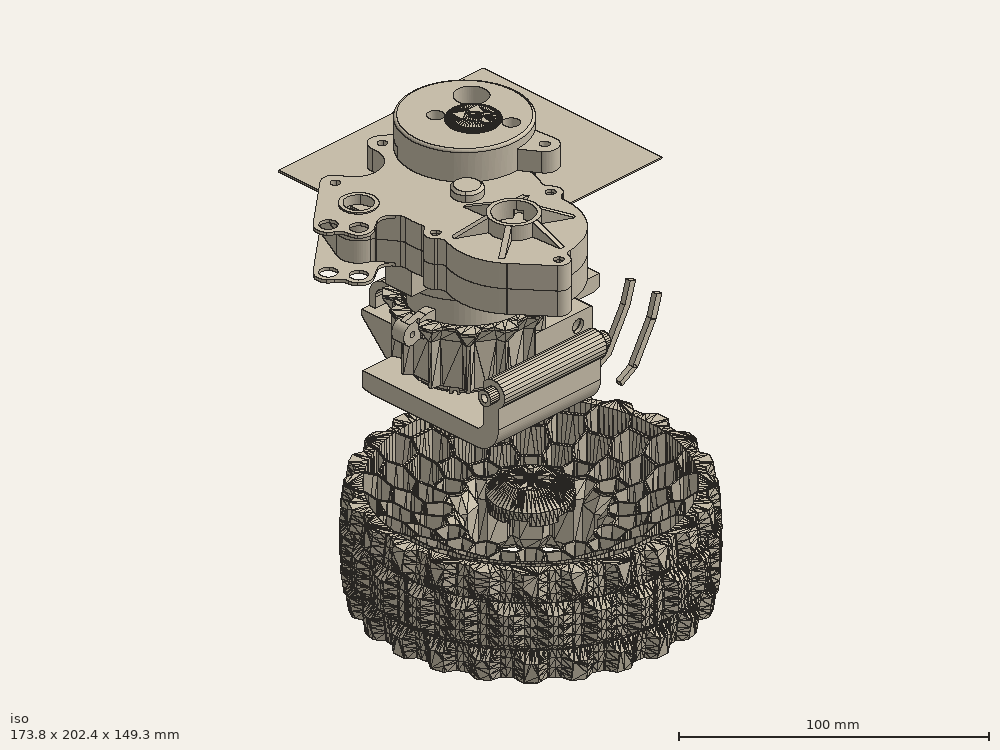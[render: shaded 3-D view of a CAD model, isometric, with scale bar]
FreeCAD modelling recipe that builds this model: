
FCSTD DOCUMENT  (FreeCAD 0.20R29410 (Git))
Label: MonsterBeetleParts
License: All rights reserved
LicenseURL: http://en.wikipedia.org/wiki/All_rights_reserved
objects: Sketcher::SketchObject×70, PartDesign::Pad×48, PartDesign::Pocket×42, Part::Feature×25, PartDesign::Fillet×22, PartDesign::Body×19, Mesh::Feature×13, Part::Box×12, PartDesign::FeatureBase×10, Part::FeaturePython×6, PartDesign::Chamfer×5, Part::MultiFuse×5, App::MeasureDistance×4, App::Part×4, App::DocumentObjectGroup×1
note: 381 computed .brp shape members not serialized (recipe doc carries the construction recipe); baked Part::Feature solids carry a one-line shape summary decoded from their .brp

FEATURE [Sketcher::SketchObject] Sketch
  FullyConstrained = true
  MapMode = 5
  Placement = pos=(0,0,0) rot=(1,0,0;1.5708rad)
  Support = -> [XZ_Plane]
  sketch-geometry (21):
    g0: Circle CenterX=0 CenterY=0 CenterZ=0 NormalX=0 NormalY=0 NormalZ=1 AngleXU=0 Radius=1.55
    g1: Circle CenterX=20 CenterY=0 CenterZ=0 NormalX=0 NormalY=0 NormalZ=1 AngleXU=0 Radius=1.55
    g2: Circle CenterX=-3 CenterY=9 CenterZ=0 NormalX=0 NormalY=0 NormalZ=1 AngleXU=0 Radius=1.05
    g3: Circle CenterX=17 CenterY=9 CenterZ=0 NormalX=0 NormalY=0 NormalZ=1 AngleXU=0 Radius=1.05
    g4: Circle CenterX=-28 CenterY=20 CenterZ=0 NormalX=0 NormalY=0 NormalZ=1 AngleXU=0 Radius=1.05
    g5: ArcOfCircle CenterX=20 CenterY=0 CenterZ=0 NormalX=0 NormalY=0 NormalZ=1 AngleXU=0 Radius=5 StartAngle=4.71239 EndAngle=7.35715
    g6: ArcOfCircle CenterX=0 CenterY=0 CenterZ=0 NormalX=0 NormalY=0 NormalZ=1 AngleXU=0 Radius=5 StartAngle=3.86723 EndAngle=4.71239
    g7: LineSegment StartX=2e-16 StartY=-5 StartZ=0 EndX=20 EndY=-5 EndZ=0
    g8: ArcOfCircle CenterX=17 CenterY=9 CenterZ=0 NormalX=0 NormalY=0 NormalZ=1 AngleXU=0 Radius=3 StartAngle=5.89015 EndAngle=8.82416
    g9: ArcOfCircle CenterX=21.6188 CenterY=7.08502 CenterZ=0 NormalX=0 NormalY=0 NormalZ=1 AngleXU=0 Radius=2 StartAngle=2.74856 EndAngle=4.21556
    g10: LineSegment StartX=20.6655 StartY=5.32683 StartZ=0 EndX=22.3832 EndY=4.3955 EndZ=0
    g11: ArcOfCircle CenterX=12.8751 CenterY=11.8258 CenterZ=0 NormalX=0 NormalY=0 NormalZ=1 AngleXU=0 Radius=2 StartAngle=4.21556 EndAngle=5.68257
    g12: ArcOfCircle CenterX=-20 CenterY=16 CenterZ=0 NormalX=0 NormalY=0 NormalZ=1 AngleXU=0 Radius=10 StartAngle=1.07397 EndAngle=1.84246
    g13: LineSegment StartX=-20 StartY=26 StartZ=0 EndX=20 EndY=26 EndZ=0
    g14: LineSegment StartX=-15.2336 StartY=24.791 StartZ=0 EndX=11.9218 EndY=10.0676 EndZ=0
    g15: LineSegment StartX=11.9218 StartY=10.0676 StartZ=0 EndX=20.6655 EndY=5.32683 EndZ=0
    g16: LineSegment StartX=-22.6834 StartY=25.6332 StartZ=0 EndX=-29.0734 EndY=23.8533 EndZ=0
    g17: ArcOfCircle CenterX=-28 CenterY=20 CenterZ=0 NormalX=0 NormalY=0 NormalZ=1 AngleXU=0 Radius=4 StartAngle=1.84246 EndAngle=5.19363
    g18: ArcOfCircle CenterX=-23.9246 CenterY=12.1957 CenterZ=0 NormalX=0 NormalY=0 NormalZ=1 AngleXU=0 Radius=4.80428 StartAngle=0.725635 EndAngle=2.05204
    g19: LineSegment StartX=-20.3307 StartY=15.3839 StartZ=0 EndX=-3.74039 EndY=-3.31805 EndZ=0
    g20: LineSegment StartX=-23.9246 StartY=17 StartZ=0 EndX=20 EndY=17 EndZ=0
  constraints (56):
    c: PointOnObject(g1,g-1)
    c: Equal(g0,g1)
    c: Diameter(g0) = 3.1
    c: Equal(g2,g3)
    c: Diameter(g2) = 2.1
    c: Diameter(g4) = 2.1
    c: Distance(g0,g1) = 20
    c: Horizontal(g3,g2)
    c: Distance(g3,g2) = 20
    c: DistanceX(g2,g0) = 3
    c: DistanceY(g0,g2) = 9
    c: DistanceY(g0,g4) = 20
    c: DistanceX(g4,g1) = 48
    c: DistanceX(g4,g2) = 25
    c: DistanceY(g2,g4) = 11
    c: Coincident(g5,g1)
    c: Distance(g1,g5) = 5
    c: Coincident(g6,g0)
    c: Distance(g0,g6) = 5
    c: Tangent(g7,g5) = -1.5708
    c: Tangent(g7,g6) = -1.5708
    c: Coincident(g8,g3)
    c: Tangent(g10,g5) = 1.5708
    c: Tangent(g10,g9) = -1.5708
    c: Distance(g9,g9) = 2
    c: Tangent(g8,g9) = 1.5708
    c: Distance(g11,g11) = 2
    c: Distance(g3,g8) = 3
    c: Tangent(g8,g11) = 1.5708
    c: Horizontal(g13)
    c: Tangent(g13,g12)
    c: Vertical(g13,g1)
    c: Distance(g13) = 40
    c: Tangent(g14,g11) = -1.5708
    c: Tangent(g14,g12) = 1.5708
    c: Coincident(g15,g11)
    c: Coincident(g15,g9)
    c: Tangent(g15,g11)
    c: Tangent(g15,g10)
    c: Distance(g13,g1) = 26
    c: Distance(g12,g12) = 10
    c: Coincident(g17,g4)
    c: Tangent(g16,g12) = -1.5708
    c: Tangent(g17,g16) = -1.5708
    c: Distance(g4,g16) = 4
    c: Tangent(g18,g17) = 1.5708
    c: Tangent(g19,g6) = -1.5708
    c: Tangent(g19,g18) = 1.5708
    c: PointOnObject(g20,g18)
    c: Horizontal(g20)
    c: Vertical(g20,g1)
    c: Tangent(g20,g18)
    c: Distance(g19) = 25
    c: Distance(g20,g1) = 17
    c: PointOnObject(g13,g12)
    c: Coincident(g0,g-1)
FEATURE [PartDesign::Pad] Pad
  Direction = (1,1,1)
  Length = 3.5
  Length2 = 100
  Placement = pos=(0,0,0) rot=(1,0,0;1.5708rad)
  Profile = -> Sketch
  Type = 0
FEATURE [Sketcher::SketchObject] Sketch001
  ExternalGeometry = -> [Pad]
  FullyConstrained = true
  MapMode = 5
  Placement = pos=(0,-3.5,8e-16) rot=(1,0,0;1.5708rad)
  Support = -> [Pad]
  sketch-geometry (8):
    g0: ArcOfCircle CenterX=-28 CenterY=20 CenterZ=0 NormalX=0 NormalY=0 NormalZ=1 AngleXU=0 Radius=4 StartAngle=5.867 EndAngle=7.19835
    g1: Circle CenterX=0 CenterY=0 CenterZ=0 NormalX=0 NormalY=0 NormalZ=1 AngleXU=0 Radius=3
    g2: Circle CenterX=20 CenterY=0 CenterZ=0 NormalX=0 NormalY=0 NormalZ=1 AngleXU=0 Radius=3
    g3: ArcOfCircle CenterX=-24.9517 CenterY=23.9633 CenterZ=0 NormalX=0 NormalY=0 NormalZ=1 AngleXU=0 Radius=1 StartAngle=1.84246 EndAngle=4.05676
    g4: ArcOfCircle CenterX=-23.4268 CenterY=17.9786 CenterZ=0 NormalX=0 NormalY=0 NormalZ=1 AngleXU=0 Radius=1 StartAngle=2.7254 EndAngle=4.62652
    g5: LineSegment StartX=-29.0734 StartY=23.8533 StartZ=0 EndX=-25.2201 EndY=24.9267 EndZ=0
    g6: ArcOfCircle CenterX=-23.9246 CenterY=12.1957 CenterZ=0 NormalX=0 NormalY=0 NormalZ=1 AngleXU=0 Radius=4.80428 StartAngle=1.48492 EndAngle=2.05204
    g7: ArcOfCircle CenterX=-28 CenterY=20 CenterZ=0 NormalX=0 NormalY=0 NormalZ=1 AngleXU=0 Radius=4 StartAngle=1.84246 EndAngle=5.19363
  constraints (21):
    c: Coincident(g0,g-3)
    c: Equal(g0,g-6)
    c: Coincident(g1,g-1)
    c: Coincident(g2,g-5)
    c: Equal(g1,g2)
    c: Diameter(g1) = 6
    c: PointOnObject(g3,g-8)
    c: Tangent(g3,g-8)
    c: Distance(g3,g3) = 1
    c: PointOnObject(g4,g-7)
    c: Tangent(g4,g-7)
    c: Distance(g4,g4) = 1
    c: Coincident(g5,g3)
    c: Coincident(g6,g-7)
    c: Coincident(g6,g4)
    c: Tangent(g0,g4) = 1.5708
    c: Coincident(g7,g6)
    c: Equal(g0,g7)
    c: Tangent(g0,g3) = 1.5708
    c: Coincident(g0,g7)
    c: Tangent(g7,g5) = 1.5708
FEATURE [PartDesign::Pocket] Pocket
  BaseFeature = -> Pad
  Direction = (1,1,1)
  Length = 1
  Length2 = 100
  Placement = pos=(0,0,0) rot=(1,0,0;1.5708rad)
  Profile = -> Sketch001
  Refine = true
  Type = 0
FEATURE [Sketcher::SketchObject] Sketch002
  ExternalGeometry = -> [Pocket]
  FullyConstrained = true
  MapMode = 5
  Placement = pos=(0,-3.5,8e-16) rot=(1,0,0;1.5708rad)
  Support = -> [Pocket]
  sketch-geometry (4):
    g0: Circle CenterX=-3 CenterY=9 CenterZ=0 NormalX=0 NormalY=0 NormalZ=1 AngleXU=0 Radius=3
    g1: Circle CenterX=17 CenterY=9 CenterZ=0 NormalX=0 NormalY=0 NormalZ=1 AngleXU=0 Radius=3
    g2: Circle CenterX=-3 CenterY=9 CenterZ=0 NormalX=0 NormalY=0 NormalZ=1 AngleXU=0 Radius=1.05
    g3: Circle CenterX=17 CenterY=9 CenterZ=0 NormalX=0 NormalY=0 NormalZ=1 AngleXU=0 Radius=1.05
  constraints (8):
    c: Coincident(g0,g-3)
    c: Coincident(g1,g-4)
    c: Equal(g1,g-5)
    c: Equal(g1,g0)
    c: Coincident(g2,g0)
    c: Coincident(g3,g1)
    c: Equal(g3,g-4)
    c: Equal(g2,g3)
FEATURE [PartDesign::Pad] Pad001
  BaseFeature = -> Pocket
  Direction = (1,1,1)
  Length = 6
  Length2 = 100
  Placement = pos=(0,0,0) rot=(1,0,0;1.5708rad)
  Profile = -> Sketch002
  Refine = true
  Type = 0
FEATURE [Sketcher::SketchObject] Sketch003
  ExternalGeometry = -> [Pad001]
  FullyConstrained = true
  MapMode = 5
  Placement = pos=(0,0,0) rot=(-1,0,0;1.5708rad)
  Support = -> [Pad001]
  sketch-geometry (2):
    g0: Circle CenterX=-28 CenterY=-20 CenterZ=0 NormalX=0 NormalY=0 NormalZ=1 AngleXU=0 Radius=4
    g1: Circle CenterX=-28 CenterY=-20 CenterZ=0 NormalX=0 NormalY=0 NormalZ=1 AngleXU=0 Radius=1.05
  constraints (4):
    c: Coincident(g0,g-4)
    c: Coincident(g1,g0)
    c: Equal(g0,g-4)
    c: Equal(g1,g-3)
FEATURE [PartDesign::Pad] Pad002
  BaseFeature = -> Pad001
  Direction = (1,1,1)
  Length = 3
  Length2 = 100
  Placement = pos=(0,0,0) rot=(1,0,0;1.5708rad)
  Profile = -> Sketch003
  Refine = true
  Type = 0
FEATURE [Sketcher::SketchObject] Sketch004
  ExternalGeometry = -> [Pad002]
  FullyConstrained = true
  MapMode = 5
  Placement = pos=(0,0,0) rot=(-1,0,0;1.5708rad)
  Support = -> [Pad002]
  sketch-geometry (4):
    g0: ArcOfCircle CenterX=-28 CenterY=-20 CenterZ=0 NormalX=0 NormalY=0 NormalZ=1 AngleXU=0 Radius=6 StartAngle=5.28179 EndAngle=6.82936
    g1: ArcOfCircle CenterX=-28 CenterY=-20 CenterZ=0 NormalX=0 NormalY=0 NormalZ=1 AngleXU=0 Radius=4 StartAngle=4.44072 EndAngle=7.37274
    g2: ArcOfCircle CenterX=-23.9246 CenterY=-12.1957 CenterZ=0 NormalX=0 NormalY=0 NormalZ=1 AngleXU=0 Radius=4.80428 StartAngle=4.23114 EndAngle=4.93309
    g3: LineSegment StartX=-29.0734 StartY=-23.8533 StartZ=0 EndX=-24.7652 EndY=-25.0533 EndZ=0
  constraints (11):
    c: Coincident(g0,g-3)
    c: Coincident(g1,g0)
    c: Equal(g1,g-3)
    c: Diameter(g0) = 12
    c: Coincident(g2,g-4)
    c: Equal(g2,g-4)
    c: PointOnObject(g3,g-5)
    c: Coincident(g0,g3)
    c: Coincident(g0,g2)
    c: Tangent(g1,g3) = -1.5708
    c: Coincident(g1,g2)
FEATURE [PartDesign::Pad] Pad003
  BaseFeature = -> Pad002
  Direction = (1,1,1)
  Length = 2
  Length2 = 100
  Placement = pos=(0,0,0) rot=(1,0,0;1.5708rad)
  Profile = -> Sketch004
  Refine = true
  Type = 0
FEATURE [PartDesign::Body] Body  label="Suspention_Arm"
  Group = -> [Sketch,Pad,Sketch001,Pocket,Sketch002,Pad001,Sketch003,Pad002,Sketch004,Pad003]
  Origin = -> Origin
  Tip = -> Pad003
FEATURE [Sketcher::SketchObject] Sketch005
  FullyConstrained = true
  MapMode = 5
  Support = -> [XY_Plane001]
  sketch-geometry (14):
    g0: LineSegment StartX=0 StartY=0 StartZ=0 EndX=60 EndY=0 EndZ=0
    g1: LineSegment StartX=60 StartY=0 StartZ=0 EndX=60 EndY=10 EndZ=0
    g2: LineSegment StartX=60 StartY=10 StartZ=0 EndX=0 EndY=10 EndZ=0
    g3: LineSegment StartX=0 StartY=10 StartZ=0 EndX=0 EndY=0 EndZ=0
    g4: Circle CenterX=13 CenterY=5 CenterZ=0 NormalX=0 NormalY=0 NormalZ=1 AngleXU=0 Radius=1.25
    g5: Circle CenterX=23 CenterY=5 CenterZ=0 NormalX=0 NormalY=0 NormalZ=1 AngleXU=0 Radius=1.25
    g6: Circle CenterX=37 CenterY=5 CenterZ=0 NormalX=0 NormalY=0 NormalZ=1 AngleXU=0 Radius=1.25
    g7: Circle CenterX=47 CenterY=5 CenterZ=0 NormalX=0 NormalY=0 NormalZ=1 AngleXU=0 Radius=1.25
    g8: LineSegment StartX=13 StartY=5 StartZ=0 EndX=13 EndY=10 EndZ=0
    g9: LineSegment StartX=13 StartY=5 StartZ=0 EndX=13 EndY=0 EndZ=0
    g10: LineSegment StartX=37 StartY=5 StartZ=0 EndX=37 EndY=10 EndZ=0
    g11: LineSegment StartX=37 StartY=5 StartZ=0 EndX=37 EndY=0 EndZ=0
    g12: LineSegment StartX=0 StartY=5 StartZ=0 EndX=13 EndY=5 EndZ=0
    g13: LineSegment StartX=47 StartY=5 StartZ=0 EndX=60 EndY=5 EndZ=0
  constraints (41):
    c: Coincident(g0,g1)
    c: Coincident(g1,g2)
    c: Coincident(g2,g3)
    c: Coincident(g3,g0)
    c: Horizontal(g0)
    c: Horizontal(g2)
    c: Vertical(g1)
    c: Vertical(g3)
    c: Coincident(g0,g-1)
    c: Distance(g2) = 60
    c: Distance(g1) = 10
    c: Horizontal(g7,g6)
    c: Horizontal(g5,g4)
    c: Equal(g4,g5)
    c: Equal(g4,g6)
    c: Equal(g4,g7)
    c: Diameter(g4) = 2.5
    c: Coincident(g8,g4)
    c: PointOnObject(g8,g2)
    c: Vertical(g8)
    c: Coincident(g9,g4)
    c: PointOnObject(g9,g0)
    c: Vertical(g9)
    c: Equal(g9,g8)
    c: Coincident(g10,g6)
    c: PointOnObject(g10,g2)
    c: Coincident(g11,g6)
    c: PointOnObject(g11,g0)
    c: Vertical(g11)
    c: Vertical(g10)
    c: Equal(g10,g11)
    c: PointOnObject(g12,g3)
    c: Coincident(g12,g4)
    c: Horizontal(g12)
    c: Coincident(g13,g7)
    c: PointOnObject(g13,g1)
    c: Horizontal(g13)
    c: Distance(g13) = 13
    c: Distance(g6,g7) = 10
    c: Distance(g4,g5) = 10
    c: Distance(g12) = 13
FEATURE [PartDesign::Pad] Pad004
  Direction = (1,1,1)
  Length = 5.9
  Length2 = 100
  Profile = -> Sketch005
  Type = 0
FEATURE [PartDesign::Chamfer] Chamfer
  Angle = 25
  Base = -> Pad004 [Edge11,Edge6]
  BaseFeature = -> Pad004
  ChamferType = 2
  FlipDirection = true
  Size = 2
  Size2 = 1
  SupportTransform = false
  UseAllEdges = false
FEATURE [PartDesign::Body] Body001  label="ServoHolder"
  Group = -> [Sketch005,Pad004,Chamfer]
  Origin = -> Origin001
  Tip = -> Chamfer
FEATURE [Mesh::Feature] battcover
FEATURE [Part::Feature] battcover001
  shape: bbox 54.7 x 80.03 x 15.89 mm, 590 faces, 0 solids (baked)
FEATURE [Part::Feature] battcover001_solid  label="battcover001 (Solid)"
  shape: bbox 54.7 x 80.03 x 15.89 mm, 590 faces (baked)
FEATURE [PartDesign::FeatureBase] BaseFeature
  BaseFeature = -> battcover001_solid
FEATURE [Sketcher::SketchObject] Sketch006
  ExternalGeometry = -> [BaseFeature]
  FullyConstrained = true
  MapMode = 5
  Placement = pos=(0,0,2.498) rot=(0,0,1;0rad)
  Support = -> [BaseFeature]
  sketch-geometry (4):
    g0: LineSegment StartX=-23.35 StartY=-27.1087 StartZ=0 EndX=23.35 EndY=-27.1087 EndZ=0
    g1: LineSegment StartX=23.35 StartY=-27.1087 StartZ=0 EndX=23.35 EndY=25.2862 EndZ=0
    g2: LineSegment StartX=23.35 StartY=25.2862 StartZ=0 EndX=-23.35 EndY=25.2862 EndZ=0
    g3: LineSegment StartX=-23.35 StartY=25.2862 StartZ=0 EndX=-23.35 EndY=-27.1087 EndZ=0
  constraints (10):
    c: Coincident(g0,g1)
    c: Coincident(g1,g2)
    c: Coincident(g2,g3)
    c: Coincident(g3,g0)
    c: Horizontal(g2)
    c: Vertical(g1)
    c: Vertical(g3)
    c: Coincident(g0,g-5)
    c: Coincident(g0,g-6)
    c: Horizontal(g1,g-8)
FEATURE [PartDesign::Pad] Pad005
  BaseFeature = -> BaseFeature
  Direction = (1,1,1)
  Length = 2
  Length2 = 10
  Profile = -> Sketch006
  Reversed = true
  Type = 4
FEATURE [Sketcher::SketchObject] Sketch007
  ExternalGeometry = -> [Pad005]
  FullyConstrained = true
  MapMode = 5
  Placement = pos=(0,-27.1087,0) rot=(1,0,0;1.5708rad)
  Support = -> [Pad005]
  sketch-geometry (4):
    g0: LineSegment StartX=-23.35 StartY=-7.502 StartZ=0 EndX=23.35 EndY=-7.502 EndZ=0
    g1: LineSegment StartX=23.35 StartY=-7.502 StartZ=0 EndX=23.35 EndY=4.498 EndZ=0
    g2: LineSegment StartX=23.35 StartY=4.498 StartZ=0 EndX=-23.35 EndY=4.498 EndZ=0
    g3: LineSegment StartX=-23.35 StartY=4.498 StartZ=0 EndX=-23.35 EndY=-7.502 EndZ=0
  constraints (11):
    c: Coincident(g0,g1)
    c: Coincident(g1,g2)
    c: Coincident(g2,g3)
    c: Coincident(g3,g0)
    c: Horizontal(g0)
    c: Horizontal(g2)
    c: Vertical(g1)
    c: Vertical(g3)
    c: Coincident(g0,g-4)
    c: Vertical(g1,g-5)
    c: Distance(g1) = 12
FEATURE [PartDesign::Pad] Pad006
  BaseFeature = -> Pad005
  Direction = (1,1,1)
  Length = 10
  Length2 = 100
  Profile = -> Sketch007
  Refine = true
  Type = 0
FEATURE [Sketcher::SketchObject] Sketch008
  ExternalGeometry = -> [Pad006]
  FullyConstrained = true
  MapMode = 5
  Placement = pos=(8.6,0,0) rot=(0.57735,0.57735,0.57735;2.0944rad)
  Support = -> [Pad006]
  sketch-geometry (3):
    g0: LineSegment StartX=25.2862 StartY=-7.502 StartZ=0 EndX=40 EndY=2 EndZ=0
    g1: LineSegment StartX=25.2862 StartY=2 StartZ=0 EndX=25.2862 EndY=-7.502 EndZ=0
    g2: LineSegment StartX=40 StartY=2 StartZ=0 EndX=25.2862 EndY=2 EndZ=0
  constraints (7):
    c: Coincident(g0,g-3)
    c: Coincident(g1,g0)
    c: Horizontal(g1,g-5)
    c: Vertical(g1)
    c: Coincident(g2,g-5)
    c: Coincident(g2,g1)
    c: Coincident(g0,g2)
FEATURE [PartDesign::Pad] Pad007
  BaseFeature = -> Pad006
  Direction = (1,1,1)
  Length = 17
  Length2 = 100
  Profile = -> Sketch008
  Reversed = true
  Type = 3
  UpToFace = -> Pad006 [Face22]
FEATURE [PartDesign::Pocket] Pocket001
  BaseFeature = -> Pad007
  Direction = (1,1,1)
  Length = 5
  Length2 = 100
  Profile = -> Pad007 [Face126]
  Type = 0
FEATURE [PartDesign::Pocket] Pocket002
  BaseFeature = -> Pocket001
  Direction = (1,1,1)
  Length = 21
  Length2 = 100
  Profile = -> Pocket001 [Face94]
  Refine = true
  Type = 0
FEATURE [PartDesign::Pocket] Pocket003
  BaseFeature = -> Pocket002
  Direction = (1,1,1)
  Length = 0.05
  Length2 = 100
  Profile = -> Pocket002 [Face81]
  Refine = true
  Type = 0
FEATURE [PartDesign::Pocket] Pocket004
  BaseFeature = -> Pocket003
  Direction = (1,1,1)
  Length = 5
  Length2 = 100
  Profile = -> Pocket003 [Face86]
  Type = 0
FEATURE [PartDesign::Pocket] Pocket005
  BaseFeature = -> Pocket004
  Direction = (1,1,1)
  Length = 5
  Length2 = 100
  Profile = -> Pocket004 [Face81]
  Refine = true
  Type = 0
FEATURE [Sketcher::SketchObject] Sketch009
  ExternalGeometry = -> [Pocket005]
  FullyConstrained = true
  MapMode = 5
  Placement = pos=(0,0,4.498) rot=(0,0,1;0rad)
  Support = -> [Pocket005]
  sketch-geometry (4):
    g0: LineSegment StartX=-23.35 StartY=-27.1087 StartZ=0 EndX=23.35 EndY=-27.1087 EndZ=0
    g1: LineSegment StartX=23.35 StartY=-27.1087 StartZ=0 EndX=23.35 EndY=24.875 EndZ=0
    g2: LineSegment StartX=23.35 StartY=24.875 StartZ=0 EndX=-23.35 EndY=24.875 EndZ=0
    g3: LineSegment StartX=-23.35 StartY=24.875 StartZ=0 EndX=-23.35 EndY=-27.1087 EndZ=0
  constraints (11):
    c: Coincident(g0,g1)
    c: Coincident(g1,g2)
    c: Coincident(g2,g3)
    c: Coincident(g3,g0)
    c: Horizontal(g0)
    c: Horizontal(g2)
    c: Vertical(g1)
    c: Vertical(g3)
    c: Coincident(g0,g-3)
    c: PointOnObject(g-4,g2)
    c: Vertical(g1,g-5)
FEATURE [PartDesign::Pocket] Pocket006
  BaseFeature = -> Pocket005
  Direction = (1,1,1)
  Length = 9
  Length2 = 100
  Profile = -> Sketch009
  Type = 0
FEATURE [PartDesign::Pocket] Pocket007
  BaseFeature = -> Pocket006
  Direction = (1,1,1)
  Length = 10
  Length2 = 100
  Profile = -> Pocket006 [Face87]
  Type = 0
FEATURE [Sketcher::SketchObject] Sketch010
  ExternalGeometry = -> [Pocket007]
  FullyConstrained = true
  MapMode = 5
  Placement = pos=(0,25.2862,0) rot=(0,0.707107,0.707107;3.14159rad)
  Support = -> [Pocket007]
  sketch-geometry (12):
    g0: LineSegment StartX=23.35 StartY=4.498 StartZ=0 EndX=5.3 EndY=4.498 EndZ=0
    g1: LineSegment StartX=5.3 StartY=4.498 StartZ=0 EndX=5.3 EndY=4.275 EndZ=0
    g2: LineSegment StartX=5.3 StartY=4.275 StartZ=0 EndX=8.7 EndY=4.275 EndZ=0
    g3: LineSegment StartX=8.7 StartY=4.275 StartZ=0 EndX=8.7 EndY=-7.502 EndZ=0
    g4: LineSegment StartX=8.7 StartY=-7.502 StartZ=0 EndX=23.35 EndY=-7.502 EndZ=0
    g5: LineSegment StartX=23.35 StartY=-7.502 StartZ=0 EndX=23.35 EndY=4.498 EndZ=0
    g6: LineSegment StartX=-5.3 StartY=4.498 StartZ=0 EndX=-5.3 EndY=4.275 EndZ=0
    g7: LineSegment StartX=-5.3 StartY=4.275 StartZ=0 EndX=-8.6 EndY=4.275 EndZ=0
    g8: LineSegment StartX=-8.6 StartY=4.275 StartZ=0 EndX=-8.6 EndY=-7.502 EndZ=0
    g9: LineSegment StartX=-8.6 StartY=-7.502 StartZ=0 EndX=-23.35 EndY=-7.502 EndZ=0
    g10: LineSegment StartX=-23.35 StartY=-7.502 StartZ=0 EndX=-23.35 EndY=4.498 EndZ=0
    g11: LineSegment StartX=-23.35 StartY=4.498 StartZ=0 EndX=-5.3 EndY=4.498 EndZ=0
  constraints (24):
    c: Coincident(g0,g-6)
    c: Coincident(g0,g-6)
    c: Coincident(g1,g0)
    c: Coincident(g1,g-7)
    c: Coincident(g2,g1)
    c: Coincident(g2,g-7)
    c: Coincident(g3,g2)
    c: Coincident(g3,g-8)
    c: Coincident(g4,g3)
    c: Coincident(g4,g-8)
    c: Coincident(g5,g4)
    c: Coincident(g5,g0)
    c: Coincident(g6,g-3)
    c: Coincident(g6,g-4)
    c: Coincident(g7,g6)
    c: Coincident(g7,g-4)
    c: Coincident(g8,g7)
    c: Coincident(g8,g-5)
    c: Coincident(g9,g8)
    c: Coincident(g9,g-5)
    c: Coincident(g10,g9)
    c: Coincident(g10,g-3)
    c: Coincident(g11,g10)
    c: Coincident(g11,g6)
FEATURE [PartDesign::Pocket] Pocket008
  BaseFeature = -> Pocket007
  Direction = (1,1,1)
  Length = 0.42
  Length2 = 100
  Profile = -> Sketch010
  Refine = true
  Type = 0
FEATURE [Sketcher::SketchObject] Sketch011
  ExternalGeometry = -> [Pocket008]
  FullyConstrained = true
  MapMode = 5
  Placement = pos=(8.6,0,0) rot=(0.57735,0.57735,0.57735;2.0944rad)
  Support = -> [Pocket008]
  sketch-geometry (3):
    g0: LineSegment StartX=24.875 StartY=-4.502 StartZ=0 EndX=21.875 EndY=-4.502 EndZ=0
    g1: LineSegment StartX=21.875 StartY=-4.502 StartZ=0 EndX=24.875 EndY=-1.502 EndZ=0
    g2: LineSegment StartX=24.875 StartY=-1.502 StartZ=0 EndX=24.875 EndY=-4.502 EndZ=0
  constraints (8):
    c: Coincident(g0,g-4)
    c: PointOnObject(g0,g-3)
    c: Coincident(g1,g0)
    c: PointOnObject(g1,g-4)
    c: Coincident(g2,g1)
    c: Coincident(g2,g0)
    c: Angle(g1,g2) = 0.785398
    c: Distance(g2) = 3
FEATURE [PartDesign::Pad] Pad008
  BaseFeature = -> Pocket008
  Direction = (1,1,1)
  Length = 10
  Length2 = 100
  Profile = -> Sketch011
  Reversed = true
  Type = 3
  UpToFace = -> Pocket008 [Face94]
FEATURE [PartDesign::Pocket] Pocket009
  BaseFeature = -> Pad008
  Direction = (1,1,1)
  Length = 3
  Length2 = 100
  Profile = -> Pad008 [Face46]
  Refine = true
  Type = 0
FEATURE [PartDesign::Chamfer] Chamfer001
  Angle = 45
  Base = -> Pocket009 [Edge230]
  BaseFeature = -> Pocket009
  ChamferType = 0
  FlipDirection = false
  Size = 3
  Size2 = 1
  SupportTransform = false
  UseAllEdges = false
FEATURE [PartDesign::Fillet] Fillet
  Base = -> Chamfer001 [Edge72]
  BaseFeature = -> Chamfer001
  Radius = 10
  SupportTransform = false
  UseAllEdges = false
FEATURE [Sketcher::SketchObject] Sketch012
  ExternalGeometry = -> [Pocket008]
  FullyConstrained = true
  MapMode = 5
  Placement = pos=(0,-2e-16,-7.502) rot=(1,0,0;3.14159rad)
  Support = -> [Pocket008]
  sketch-geometry (4):
    g0: LineSegment StartX=23.35 StartY=37.1087 StartZ=0 EndX=-23.35 EndY=37.1087 EndZ=0
    g1: LineSegment StartX=-23.35 StartY=37.1087 StartZ=0 EndX=-23.35 EndY=-24.8662 EndZ=0
    g2: LineSegment StartX=-23.35 StartY=-24.8662 StartZ=0 EndX=23.35 EndY=-24.8662 EndZ=0
    g3: LineSegment StartX=23.35 StartY=-24.8662 StartZ=0 EndX=23.35 EndY=37.1087 EndZ=0
  constraints (10):
    c: Coincident(g0,g1)
    c: Coincident(g1,g2)
    c: Coincident(g2,g3)
    c: Coincident(g3,g0)
    c: Horizontal(g0)
    c: Horizontal(g2)
    c: Vertical(g1)
    c: Vertical(g3)
    c: Coincident(g0,g-4)
    c: Coincident(g1,g-3)
FEATURE [PartDesign::Pad] Pad009
  BaseFeature = -> Fillet
  Direction = (1,1,1)
  Length = 6
  Length2 = 12
  Profile = -> Sketch012
  Type = 4
FEATURE [Sketcher::SketchObject] Sketch013
  ExternalGeometry = -> [Pad009]
  FullyConstrained = true
  MapMode = 5
  Placement = pos=(8.6,3e-16,2e-16) rot=(0.57735,0.57735,0.57735;2.0944rad)
  Support = -> [Pad009]
  sketch-geometry (4):
    g0: LineSegment StartX=40 StartY=2 StartZ=0 EndX=24.8662 EndY=-13.502 EndZ=0
    g1: LineSegment StartX=24.8662 StartY=-13.502 StartZ=0 EndX=24.8662 EndY=4.275 EndZ=0
    g2: LineSegment StartX=24.8662 StartY=4.275 StartZ=0 EndX=40 EndY=4.275 EndZ=0
    g3: LineSegment StartX=40 StartY=4.275 StartZ=0 EndX=40 EndY=2 EndZ=0
  constraints (9):
    c: Coincident(g0,g-5)
    c: Coincident(g0,g-3)
    c: Coincident(g1,g0)
    c: Coincident(g2,g-4)
    c: Coincident(g3,g2)
    c: Coincident(g3,g0)
    c: PointOnObject(g1,g-6)
    c: Horizontal(g1,g-4)
    c: Coincident(g2,g1)
FEATURE [PartDesign::Pad] Pad010
  BaseFeature = -> Pad009
  Direction = (1,1,1)
  Length = 10
  Length2 = 100
  Profile = -> Sketch013
  Reversed = true
  Type = 3
  UpToFace = -> Pad009 [Face65]
FEATURE [Sketcher::SketchObject] Sketch014
  ExternalGeometry = -> [Pad010]
  FullyConstrained = true
  MapMode = 5
  Placement = pos=(0,1e-16,4.498) rot=(0,0,1;0rad)
  Support = -> [Pad010]
  sketch-geometry (4):
    g0: LineSegment StartX=-23.35 StartY=24.8662 StartZ=0 EndX=23.35 EndY=24.8662 EndZ=0
    g1: LineSegment StartX=23.35 StartY=24.8662 StartZ=0 EndX=23.35 EndY=-30.1087 EndZ=0
    g2: LineSegment StartX=23.35 StartY=-30.1087 StartZ=0 EndX=-23.35 EndY=-30.1087 EndZ=0
    g3: LineSegment StartX=-23.35 StartY=-30.1087 StartZ=0 EndX=-23.35 EndY=24.8662 EndZ=0
  constraints (10):
    c: Coincident(g0,g1)
    c: Coincident(g1,g2)
    c: Coincident(g2,g3)
    c: Horizontal(g0)
    c: Horizontal(g2)
    c: Vertical(g1)
    c: Vertical(g3)
    c: Coincident(g1,g-4)
    c: Coincident(g0,g-5)
    c: Coincident(g3,g0)
FEATURE [PartDesign::Pocket] Pocket010
  BaseFeature = -> Pad010
  Direction = (1,1,1)
  Length = 11
  Length2 = 100
  Profile = -> Sketch014
  Refine = true
  Type = 0
FEATURE [PartDesign::Chamfer] Chamfer002
  Angle = 45
  Base = -> Pocket010 [Edge152,Edge150]
  BaseFeature = -> Pocket010
  ChamferType = 0
  FlipDirection = false
  Size = 2
  Size2 = 1
  SupportTransform = false
  UseAllEdges = false
FEATURE [PartDesign::Fillet] Fillet001
  Base = -> Chamfer002 [Edge61,Edge64]
  BaseFeature = -> Chamfer002
  Radius = 10
  SupportTransform = false
  UseAllEdges = false
FEATURE [PartDesign::Pocket] Pocket011
  BaseFeature = -> Fillet001
  Direction = (1,1,1)
  Length = 15
  Length2 = 100
  Profile = -> Fillet001 [Face53]
  Type = 0
FEATURE [PartDesign::Pocket] Pocket012
  BaseFeature = -> Pocket011
  Direction = (1,1,1)
  Length = 15
  Length2 = 100
  Profile = -> Pocket011 [Face50]
  Type = 0
FEATURE [Sketcher::SketchObject] Sketch015
  ExternalGeometry = -> [Pocket012]
  FullyConstrained = true
  MapMode = 5
  Placement = pos=(27.35,0,0) rot=(0.57735,0.57735,0.57735;2.0944rad)
  Support = -> [Pocket012]
  sketch-geometry (3):
    g0: LineSegment StartX=-34.814 StartY=11.97 StartZ=0 EndX=-34.814 EndY=6.17 EndZ=0
    g1: LineSegment StartX=-37.715 StartY=9.07 StartZ=0 EndX=-31.914 EndY=9.07 EndZ=0
    g2: Circle CenterX=-34.814 CenterY=9.07 CenterZ=0 NormalX=0 NormalY=0 NormalZ=1 AngleXU=0 Radius=1.5
  constraints (7):
    c: Coincident(g0,g-3)
    c: Coincident(g0,g-4)
    c: Coincident(g1,g-5)
    c: Coincident(g1,g-6)
    c: PointOnObject(g2,g1)
    c: PointOnObject(g2,g0)
    c: Diameter(g2) = 3
FEATURE [PartDesign::Pocket] Pocket013
  BaseFeature = -> Pocket012
  Direction = (1,1,1)
  Length = 0
  Length2 = 100
  Profile = -> Sketch015
  Type = 3
  UpToFace = -> Pocket012 [Face89]
FEATURE [PartDesign::Body] Body002  label="BatteryCoverV1"
  BaseFeature = -> battcover001_solid
  Group = -> [BaseFeature,Sketch006,Pad005,Sketch007,Pad006,Sketch008,Pad007,Pocket001,Pocket002,Pocket003,Pocket004,Pocket005,Sketch009,Pocket006,Pocket007,Sketch010,Pocket008,Sketch011,Pad008,Pocket009,Chamfer001,Fillet,Sketch012,Pad009,Sketch013,Pad010,Sketch014,Pocket010,Chamfer002,Fillet001,Pocket011,Pocket012,Sketch015,Pocket013]
  Origin = -> Origin002
  Tip = -> Pocket013
FEATURE [Mesh::Feature] rc_car_parts_for_tamiya_Battery_cap  label="rc_car_parts_for_tamiya-Battery_cap"
FEATURE [Part::Feature] rc_car_parts_for_tamiya_Battery_cap001
  shape: bbox 38.67 x 9 x 25 mm, 2564 faces, 0 solids (baked)
FEATURE [Part::Feature] rc_car_parts_for_tamiya_Battery_cap001_solid  label="rc_car_parts_for_tamiya_Battery_cap001 (Solid)"
  Placement = pos=(19.4,0,-15) rot=(0,0,1;0rad)
  shape: bbox 38.67 x 9 x 25 mm, 2564 faces (baked)
FEATURE [Sketcher::SketchObject] Sketch016
  FullyConstrained = true
  MapMode = 5
  Placement = pos=(0,0,0) rot=(1,0,0;1.5708rad)
  Support = -> [XZ_Plane003]
  sketch-geometry (4):
    g0: LineSegment StartX=0 StartY=0 StartZ=0 EndX=38.75 EndY=0 EndZ=0
    g1: LineSegment StartX=38.75 StartY=0 StartZ=0 EndX=38.75 EndY=10 EndZ=0
    g2: LineSegment StartX=38.75 StartY=10 StartZ=0 EndX=0 EndY=10 EndZ=0
    g3: LineSegment StartX=0 StartY=10 StartZ=0 EndX=0 EndY=0 EndZ=0
  constraints (11):
    c: Coincident(g0,g1)
    c: Coincident(g1,g2)
    c: Coincident(g2,g3)
    c: Coincident(g3,g0)
    c: Horizontal(g0)
    c: Horizontal(g2)
    c: Vertical(g1)
    c: Vertical(g3)
    c: Coincident(g0,g-1)
    c: Distance(g2) = 38.75
    c: Distance(g1) = 10
FEATURE [PartDesign::Pad] Pad011
  Direction = (1,1,1)
  Length = 18
  Length2 = 100
  Placement = pos=(0,0,0) rot=(1,0,0;1.5708rad)
  Profile = -> Sketch016
  Type = 0
FEATURE [Sketcher::SketchObject] Sketch017
  ExternalGeometry = -> [Pad011]
  FullyConstrained = true
  MapMode = 5
  Placement = pos=(0,0,0) rot=(-1,0,0;1.5708rad)
  Support = -> [Pad011]
  sketch-geometry (2):
    g0: Circle CenterX=6.65 CenterY=-5 CenterZ=0 NormalX=0 NormalY=0 NormalZ=1 AngleXU=0 Radius=2.5
    g1: Circle CenterX=32.15 CenterY=-5 CenterZ=0 NormalX=0 NormalY=0 NormalZ=1 AngleXU=0 Radius=2.5
  constraints (7):
    c: Distance(g-3) = 10
    c: Distance(g0,g-3) = 6.65
    c: Distance(g0,g-4) = 5
    c: Distance(g1,g-4) = 5
    c: Distance(g1,g0) = 25.5
    c: Equal(g0,g1)
    c: Diameter(g0) = 5
FEATURE [PartDesign::Pocket] Pocket014
  BaseFeature = -> Pad011
  Direction = (1,1,1)
  Length = 0
  Length2 = 100
  Placement = pos=(0,0,0) rot=(1,0,0;1.5708rad)
  Profile = -> Sketch017
  Type = 3
  UpToFace = -> Pad011 [Face6]
FEATURE [Sketcher::SketchObject] Sketch018
  ExternalGeometry = -> [Pocket014]
  FullyConstrained = true
  MapMode = 5
  Placement = pos=(0,0,0) rot=(-1,0,0;1.5708rad)
  Support = -> [Pocket014]
  sketch-geometry (2):
    g0: Circle CenterX=6.65 CenterY=-5 CenterZ=0 NormalX=0 NormalY=0 NormalZ=1 AngleXU=0 Radius=4
    g1: Circle CenterX=32.15 CenterY=-5 CenterZ=0 NormalX=0 NormalY=0 NormalZ=1 AngleXU=0 Radius=4
  constraints (4):
    c: Coincident(g0,g-3)
    c: Coincident(g1,g-4)
    c: Diameter(g0) = 8
    c: Equal(g1,g0)
FEATURE [PartDesign::Pocket] Pocket015
  BaseFeature = -> Pocket014
  Direction = (1,1,1)
  Length = 15
  Length2 = 100
  Placement = pos=(0,0,0) rot=(1,0,0;1.5708rad)
  Profile = -> Sketch018
  Type = 0
FEATURE [Sketcher::SketchObject] Sketch019
  ExternalGeometry = -> [Pocket015]
  FullyConstrained = true
  MapMode = 5
  Placement = pos=(0,4.4e-15,10) rot=(0,0,1;3.14159rad)
  Support = -> [Pocket015]
  sketch-geometry (6):
    g0: LineSegment StartX=-26.875 StartY=0 StartZ=0 EndX=-11.875 EndY=0 EndZ=0
    g1: LineSegment StartX=-11.875 StartY=0 StartZ=0 EndX=-11.875 EndY=-5 EndZ=0
    g2: LineSegment StartX=-11.875 StartY=-5 StartZ=0 EndX=-26.875 EndY=-5 EndZ=0
    g3: LineSegment StartX=-26.875 StartY=-5 StartZ=0 EndX=-26.875 EndY=0 EndZ=0
    g4: LineSegment StartX=-26.875 StartY=0 StartZ=0 EndX=-38.75 EndY=0 EndZ=0
    g5: LineSegment StartX=-11.875 StartY=0 StartZ=0 EndX=0 EndY=0 EndZ=0
  constraints (16):
    c: Coincident(g0,g1)
    c: Coincident(g1,g2)
    c: Coincident(g2,g3)
    c: Coincident(g3,g0)
    c: Horizontal(g0)
    c: Horizontal(g2)
    c: Vertical(g1)
    c: Vertical(g3)
    c: PointOnObject(g0,g-3)
    c: Distance(g0) = 15
    c: Coincident(g4,g0)
    c: Coincident(g4,g-5)
    c: Coincident(g5,g0)
    c: Coincident(g5,g-1)
    c: Equal(g5,g4)
    c: Distance(g1) = 5
FEATURE [PartDesign::Pad] Pad012
  BaseFeature = -> Pocket015
  Direction = (1,1,1)
  Length = 30
  Length2 = 100
  Placement = pos=(0,0,0) rot=(1,0,0;1.5708rad)
  Profile = -> Sketch019
  Reversed = true
  Type = 0
FEATURE [PartDesign::Pad] Pad013
  BaseFeature = -> Pad012
  Direction = (1,1,1)
  Length = 5
  Length2 = 100
  Placement = pos=(0,0,0) rot=(1,0,0;1.5708rad)
  Profile = -> Pad012 [Face6]
  Type = 0
FEATURE [PartDesign::Pad] Pad014
  BaseFeature = -> Pad013
  Direction = (1,1,1)
  Length = 5
  Length2 = 100
  Placement = pos=(0,0,0) rot=(1,0,0;1.5708rad)
  Profile = -> Pad013 [Face4]
  Refine = true
  Type = 0
FEATURE [PartDesign::Fillet] Fillet002
  Base = -> Pad014 [Edge10,Edge5]
  BaseFeature = -> Pad014
  Placement = pos=(0,0,0) rot=(1,0,0;1.5708rad)
  Radius = 11
  SupportTransform = false
  UseAllEdges = false
FEATURE [PartDesign::Fillet] Fillet003
  Base = -> Fillet002 [Edge15,Edge11]
  BaseFeature = -> Fillet002
  Placement = pos=(0,0,0) rot=(1,0,0;1.5708rad)
  Radius = 2
  Refine = true
  SupportTransform = false
  UseAllEdges = false
FEATURE [PartDesign::Fillet] Fillet004
  Base = -> Fillet003 [Edge7]
  BaseFeature = -> Fillet003
  Placement = pos=(0,0,0) rot=(1,0,0;1.5708rad)
  Radius = 2
  SupportTransform = false
  UseAllEdges = false
FEATURE [PartDesign::Fillet] Fillet005
  Base = -> Fillet004 [Edge45,Edge51,Edge38,Edge36]
  BaseFeature = -> Fillet004
  Placement = pos=(0,0,0) rot=(1,0,0;1.5708rad)
  Radius = 0.8
  SupportTransform = false
  UseAllEdges = false
FEATURE [PartDesign::Chamfer] Chamfer003
  Angle = 45
  Base = -> Fillet005 [Edge70,Edge68]
  BaseFeature = -> Fillet005
  ChamferType = 0
  FlipDirection = false
  Placement = pos=(0,0,0) rot=(1,0,0;1.5708rad)
  Refine = true
  Size = 1.499
  Size2 = 1
  SupportTransform = false
  UseAllEdges = false
FEATURE [PartDesign::Body] Body003  label="BattSideHolder001"
  Group = -> [Sketch016,Pad011,Sketch017,Pocket014,Sketch018,Pocket015,Sketch019,Pad012,Pad013,Pad014,Fillet002,Fillet003,Fillet004,Fillet005,Chamfer003]
  Origin = -> Origin003
  Tip = -> Chamfer003
FEATURE [Sketcher::SketchObject] Sketch020
  FullyConstrained = true
  MapMode = 5
  Placement = pos=(0,0,0) rot=(1,0,0;1.5708rad)
  Support = -> [XZ_Plane004]
  sketch-geometry (4):
    g0: LineSegment StartX=0 StartY=0 StartZ=0 EndX=38.75 EndY=0 EndZ=0
    g1: LineSegment StartX=38.75 StartY=0 StartZ=0 EndX=38.75 EndY=10 EndZ=0
    g2: LineSegment StartX=38.75 StartY=10 StartZ=0 EndX=0 EndY=10 EndZ=0
    g3: LineSegment StartX=0 StartY=10 StartZ=0 EndX=0 EndY=0 EndZ=0
  constraints (11):
    c: Coincident(g0,g1)
    c: Coincident(g1,g2)
    c: Coincident(g2,g3)
    c: Coincident(g3,g0)
    c: Horizontal(g0)
    c: Horizontal(g2)
    c: Vertical(g1)
    c: Vertical(g3)
    c: Coincident(g0,g-1)
    c: Distance(g2) = 38.75
    c: Distance(g1) = 10
FEATURE [PartDesign::Pad] Pad015
  Direction = (1,1,1)
  Length = 10
  Length2 = 100
  Placement = pos=(0,0,0) rot=(1,0,0;1.5708rad)
  Profile = -> Sketch020
  Type = 0
FEATURE [Sketcher::SketchObject] Sketch021
  ExternalGeometry = -> [Pad015]
  FullyConstrained = true
  MapMode = 5
  Placement = pos=(0,0,0) rot=(-1,0,0;1.5708rad)
  Support = -> [Pad015]
  sketch-geometry (2):
    g0: Circle CenterX=6.65 CenterY=-5 CenterZ=0 NormalX=0 NormalY=0 NormalZ=1 AngleXU=0 Radius=2.5
    g1: Circle CenterX=32.15 CenterY=-5 CenterZ=0 NormalX=0 NormalY=0 NormalZ=1 AngleXU=0 Radius=2.5
  constraints (7):
    c: Distance(g-3) = 10
    c: Distance(g0,g-3) = 6.65
    c: Distance(g0,g-4) = 5
    c: Distance(g1,g-4) = 5
    c: Distance(g1,g0) = 25.5
    c: Equal(g0,g1)
    c: Diameter(g0) = 5
FEATURE [PartDesign::Pocket] Pocket016
  BaseFeature = -> Pad015
  Direction = (1,1,1)
  Length = 0
  Length2 = 100
  Placement = pos=(0,0,0) rot=(1,0,0;1.5708rad)
  Profile = -> Sketch021
  Type = 3
  UpToFace = -> Pad015 [Face6]
FEATURE [Sketcher::SketchObject] Sketch022
  ExternalGeometry = -> [Pocket016]
  FullyConstrained = true
  MapMode = 5
  Placement = pos=(0,0,0) rot=(-1,0,0;1.5708rad)
  Support = -> [Pocket016]
  sketch-geometry (2):
    g0: Circle CenterX=6.65 CenterY=-5 CenterZ=0 NormalX=0 NormalY=0 NormalZ=1 AngleXU=0 Radius=4
    g1: Circle CenterX=32.15 CenterY=-5 CenterZ=0 NormalX=0 NormalY=0 NormalZ=1 AngleXU=0 Radius=4
  constraints (4):
    c: Coincident(g0,g-3)
    c: Coincident(g1,g-4)
    c: Diameter(g0) = 8
    c: Equal(g1,g0)
FEATURE [PartDesign::Pocket] Pocket017
  BaseFeature = -> Pocket016
  Direction = (1,1,1)
  Length = 7
  Length2 = 100
  Placement = pos=(0,0,0) rot=(1,0,0;1.5708rad)
  Profile = -> Sketch022
  Type = 0
FEATURE [Sketcher::SketchObject] Sketch023
  ExternalGeometry = -> [Pocket017]
  FullyConstrained = true
  MapMode = 5
  Placement = pos=(0,0,10) rot=(0,0,1;3.14159rad)
  Support = -> [Pocket017]
  sketch-geometry (6):
    g0: LineSegment StartX=-26.875 StartY=0 StartZ=0 EndX=-11.875 EndY=0 EndZ=0
    g1: LineSegment StartX=-11.875 StartY=0 StartZ=0 EndX=-11.875 EndY=-5 EndZ=0
    g2: LineSegment StartX=-11.875 StartY=-5 StartZ=0 EndX=-26.875 EndY=-5 EndZ=0
    g3: LineSegment StartX=-26.875 StartY=-5 StartZ=0 EndX=-26.875 EndY=0 EndZ=0
    g4: LineSegment StartX=-26.875 StartY=0 StartZ=0 EndX=-38.75 EndY=0 EndZ=0
    g5: LineSegment StartX=-11.875 StartY=0 StartZ=0 EndX=0 EndY=0 EndZ=0
  constraints (16):
    c: Coincident(g0,g1)
    c: Coincident(g1,g2)
    c: Coincident(g2,g3)
    c: Coincident(g3,g0)
    c: Horizontal(g0)
    c: Horizontal(g2)
    c: Vertical(g1)
    c: Vertical(g3)
    c: PointOnObject(g0,g-3)
    c: Distance(g0) = 15
    c: Coincident(g4,g0)
    c: Coincident(g4,g-5)
    c: Coincident(g5,g0)
    c: Coincident(g5,g-1)
    c: Equal(g5,g4)
    c: Distance(g1) = 5
FEATURE [PartDesign::Pad] Pad016
  BaseFeature = -> Pocket017
  Direction = (1,1,1)
  Length = 30
  Length2 = 100
  Placement = pos=(0,0,0) rot=(1,0,0;1.5708rad)
  Profile = -> Sketch023
  Reversed = true
  Type = 0
FEATURE [PartDesign::Pad] Pad017
  BaseFeature = -> Pad016
  Direction = (1,1,1)
  Length = 5
  Length2 = 100
  Placement = pos=(0,0,0) rot=(1,0,0;1.5708rad)
  Profile = -> Pad016 [Face6]
  Type = 0
FEATURE [PartDesign::Pad] Pad018
  BaseFeature = -> Pad017
  Direction = (1,1,1)
  Length = 5
  Length2 = 100
  Placement = pos=(0,0,0) rot=(1,0,0;1.5708rad)
  Profile = -> Pad017 [Face4]
  Refine = true
  Type = 0
FEATURE [PartDesign::Fillet] Fillet006
  Base = -> Pad018 [Edge10,Edge5]
  BaseFeature = -> Pad018
  Placement = pos=(0,0,0) rot=(1,0,0;1.5708rad)
  Radius = 11
  SupportTransform = false
  UseAllEdges = false
FEATURE [PartDesign::Pad] Pad019
  BaseFeature = -> Fillet006
  Direction = (1,1,1)
  Length = 10
  Length2 = 100
  Placement = pos=(0,0,0) rot=(1,0,0;1.5708rad)
  Profile = -> Fillet006 [Face4]
  Type = 0
FEATURE [Sketcher::SketchObject] Sketch024
  ExternalGeometry = -> [Pad019]
  FullyConstrained = false
  MapMode = 5
  Placement = pos=(0,5,-1.8e-15) rot=(-1,0,0;1.5708rad)
  Support = -> [Pad019]
  sketch-geometry (12):
    g0: ArcOfCircle CenterX=6.65 CenterY=-5 CenterZ=0 NormalX=0 NormalY=0 NormalZ=1 AngleXU=0 Radius=5 StartAngle=1.98027 EndAngle=4.71239
    g1: ArcOfCircle CenterX=32.15 CenterY=-5 CenterZ=0 NormalX=0 NormalY=0 NormalZ=1 AngleXU=0 Radius=5 StartAngle=4.71239 EndAngle=7.44767
    g2: ArcOfCircle CenterX=-0.118151 CenterY=10.5946 CenterZ=0 NormalX=0 NormalY=0 NormalZ=1 AngleXU=0 Radius=12 StartAngle=5.12186 EndAngle=6.31697
    g3: ArcOfCircle CenterX=38.8689 CenterY=10.6159 CenterZ=0 NormalX=0 NormalY=0 NormalZ=1 AngleXU=0 Radius=12 StartAngle=3.10958 EndAngle=4.30607
    g4: ArcOfCircle CenterX=0.874998 CenterY=11 CenterZ=0 NormalX=0 NormalY=0 NormalZ=1 AngleXU=0 Radius=11 StartAngle=4.71239 EndAngle=6.28319
    g5: LineSegment StartX=0.875 StartY=3.6e-15 StartZ=0 EndX=0 EndY=0 EndZ=0
    g6: LineSegment StartX=0 StartY=0 StartZ=0 EndX=0 EndY=-10 EndZ=0
    g7: LineSegment StartX=0 StartY=-10 StartZ=0 EndX=6.65 EndY=-10 EndZ=0
    g8: LineSegment StartX=37.875 StartY=3.6e-15 StartZ=0 EndX=38.75 EndY=1.1e-15 EndZ=0
    g9: LineSegment StartX=38.75 StartY=1.1e-15 StartZ=0 EndX=38.75 EndY=-10 EndZ=0
    g10: LineSegment StartX=32.15 StartY=-10 StartZ=0 EndX=38.75 EndY=-10 EndZ=0
    g11: ArcOfCircle CenterX=37.875 CenterY=11 CenterZ=0 NormalX=0 NormalY=0 NormalZ=1 AngleXU=0 Radius=11 StartAngle=3.14159 EndAngle=4.71239
  constraints (26):
    c: Coincident(g0,g-11)
    c: Tangent(g0,g-3)
    c: Coincident(g1,g-10)
    c: Tangent(g1,g-3)
    c: Coincident(g5,g4)
    c: Coincident(g5,g-1)
    c: Coincident(g6,g5)
    c: Coincident(g6,g-4)
    c: Coincident(g7,g6)
    c: Coincident(g8,g-9)
    c: Coincident(g9,g8)
    c: Coincident(g9,g-5)
    c: Coincident(g10,g9)
    c: Tangent(g0,g2) = 1.5708
    c: Tangent(g1,g3) = 1.5708
    c: Coincident(g3,g-13)
    c: Coincident(g11,g3)
    c: Coincident(g4,g-12)
    c: Coincident(g2,g4)
    c: Coincident(g4,g-8)
    c: Distance(g2,g0) = 12
    c: Coincident(g11,g8)
    c: Coincident(g8,g-9)
    c: Distance(g1,g3) = 12
    c: Coincident(g0,g7)
    c: Coincident(g1,g10)
FEATURE [App::MeasureDistance] Distance  label="Distance: 0,99 mm"
  Distance = 0.992477
  P1 = (28.1446,5,4.88495)
  P2 = (27.1521,5,4.88967)
FEATURE [PartDesign::Pocket] Pocket018
  BaseFeature = -> Pad019
  Direction = (1,1,1)
  Length = 15
  Length2 = 100
  Placement = pos=(0,0,0) rot=(1,0,0;1.5708rad)
  Profile = -> Sketch024
  Refine = true
  Type = 0
FEATURE [PartDesign::Fillet] Fillet007
  Base = -> Pocket018 [Edge4,Edge2]
  BaseFeature = -> Pocket018
  Placement = pos=(0,0,0) rot=(1,0,0;1.5708rad)
  Radius = 7
  SupportTransform = false
  UseAllEdges = false
FEATURE [Sketcher::SketchObject] Sketch025
  ExternalGeometry = -> [Fillet007]
  FullyConstrained = true
  MapMode = 5
  Placement = pos=(0,5,-2.8e-15) rot=(-1,0,0;1.5708rad)
  Support = -> [Fillet007]
  sketch-geometry (4):
    g0: ArcOfCircle CenterX=32.15 CenterY=-5 CenterZ=0 NormalX=0 NormalY=0 NormalZ=1 AngleXU=0 Radius=5 StartAngle=4.02114 EndAngle=4.71239
    g1: ArcOfCircle CenterX=6.65 CenterY=-5 CenterZ=0 NormalX=0 NormalY=0 NormalZ=1 AngleXU=0 Radius=5 StartAngle=4.71239 EndAngle=5.40364
    g2: ArcOfCircle CenterX=19.4 CenterY=-20.409 CenterZ=0 NormalX=0 NormalY=0 NormalZ=1 AngleXU=0 Radius=15 StartAngle=0.879547 EndAngle=2.26205
    g3: LineSegment StartX=6.65 StartY=-10 StartZ=0 EndX=32.15 EndY=-10 EndZ=0
  constraints (9):
    c: Coincident(g0,g-5)
    c: Coincident(g1,g-4)
    c: Coincident(g1,g-4)
    c: Coincident(g0,g-5)
    c: Tangent(g2,g0) = 1.5708
    c: Tangent(g2,g1) = 1.5708
    c: Distance(g2,g0) = 15
    c: Coincident(g3,g1)
    c: Coincident(g3,g0)
FEATURE [PartDesign::Pocket] Pocket019
  BaseFeature = -> Fillet007
  Direction = (1,1,1)
  Length = 16
  Length2 = 100
  Placement = pos=(0,0,0) rot=(1,0,0;1.5708rad)
  Profile = -> Sketch025
  Refine = true
  Type = 0
FEATURE [Sketcher::SketchObject] Sketch026
  AttachmentOffset = pos=(0,0,-5) rot=(0,0,1;0rad)
  ExternalGeometry = -> [Pocket019]
  FullyConstrained = true
  MapMode = 5
  Placement = pos=(21.875,0,1.1e-15) rot=(0.707107,0,0.707107;3.14159rad)
  Support = -> [Pocket019]
  sketch-geometry (8):
    g0: LineSegment StartX=-23 StartY=-5 StartZ=0 EndX=-23 EndY=-10 EndZ=0
    g1: LineSegment StartX=-23 StartY=-10 StartZ=0 EndX=-4 EndY=-10 EndZ=0
    g2: LineSegment StartX=-4 StartY=-10 StartZ=0 EndX=-4 EndY=-5 EndZ=0
    g3: LineSegment StartX=-4 StartY=-5 StartZ=0 EndX=-6 EndY=-5 EndZ=0
    g4: LineSegment StartX=-6 StartY=-5 StartZ=0 EndX=-6 EndY=-8 EndZ=0
    g5: LineSegment StartX=-6 StartY=-8 StartZ=0 EndX=-21 EndY=-8 EndZ=0
    g6: LineSegment StartX=-21 StartY=-8 StartZ=0 EndX=-21 EndY=-5 EndZ=0
    g7: LineSegment StartX=-21 StartY=-5 StartZ=0 EndX=-23 EndY=-5 EndZ=0
  constraints (23):
    c: Vertical(g0)
    c: Coincident(g1,g0)
    c: Horizontal(g1)
    c: Coincident(g2,g1)
    c: Vertical(g2)
    c: Coincident(g3,g2)
    c: PointOnObject(g3,g-6)
    c: Horizontal(g3)
    c: Coincident(g4,g3)
    c: Vertical(g4)
    c: Coincident(g5,g4)
    c: Horizontal(g5)
    c: Coincident(g6,g5)
    c: PointOnObject(g6,g-6)
    c: Vertical(g6)
    c: Coincident(g7,g6)
    c: Coincident(g7,g0)
    c: Distance(g7) = 2
    c: Distance(g3) = 2
    c: Distance(g4,g1) = 2
    c: Distance(g5) = 15
    c: Distance(g6) = 3
    c: Coincident(g0,g-6)
FEATURE [PartDesign::Pad] Pad020
  BaseFeature = -> Pocket019
  Direction = (1,1,1)
  Length = 5
  Length2 = 100
  Placement = pos=(0,0,0) rot=(1,0,0;1.5708rad)
  Profile = -> Sketch026
  Reversed = true
  Type = 0
FEATURE [PartDesign::Fillet] Fillet008
  Base = -> Pad020 [Edge26,Edge28,Edge32,Edge34]
  BaseFeature = -> Pad020
  Placement = pos=(0,0,0) rot=(1,0,0;1.5708rad)
  Radius = 3
  SupportTransform = false
  UseAllEdges = false
FEATURE [PartDesign::Fillet] Fillet009
  Base = -> Fillet008 [Edge81,Edge83]
  BaseFeature = -> Fillet008
  Placement = pos=(0,0,0) rot=(1,0,0;1.5708rad)
  Radius = 1
  SupportTransform = false
  UseAllEdges = false
FEATURE [PartDesign::Fillet] Fillet010
  Base = -> Fillet009 [Edge14,Edge52]
  BaseFeature = -> Fillet009
  Placement = pos=(0,0,0) rot=(1,0,0;1.5708rad)
  Radius = 0.99
  SupportTransform = false
  UseAllEdges = false
FEATURE [PartDesign::Body] Body004  label="BattSideHolder002"
  Group = -> [Sketch020,Pad015,Sketch021,Pocket016,Sketch022,Pocket017,Sketch023,Pad016,Pad017,Pad018,Fillet006,Pad019,Sketch024,Pocket018,Fillet007,Sketch025,Pocket019,Sketch026,Pad020,Fillet008,Fillet009,Fillet010]
  Origin = -> Origin004
  Tip = -> Fillet010
FEATURE [Mesh::Feature] _1_R_Bumper_210807  label="01.R_Bumper_210807"
FEATURE [Part::Feature] _1_R_Bumper_210807001
  shape: bbox 68.5 x 60 x 30 mm, 1612 faces, 0 solids (baked)
FEATURE [Part::Box] Box  label="Cube"
  AttacherType = Attacher::AttachEngine3D
  Height = 17
  Length = 2.5
  Placement = pos=(51.134,-12,-15.5) rot=(0,1,0;0.523599rad)
  Width = 2
FEATURE [Part::Box] Box003  label="Cube003"
  AttacherType = Attacher::AttachEngine3D
  Height = 9
  Length = 2.5
  Placement = pos=(59.4048,-12,-1.40558) rot=(0,1,0;0.296706rad)
  Width = 2
FEATURE [Part::Box] Box004  label="Cube004"
  AttacherType = Attacher::AttachEngine3D
  Height = 8
  Length = 2
  Placement = pos=(53.299,-12,-16.75) rot=(0,1,0;4.18879rad)
  Width = 2
FEATURE [Part::MultiFuse] Fusion
  Refine = true
  Shapes = -> [Box,Box003,Box004]
FEATURE [Part::Box] Box006  label="Cube006"
  AttacherType = Attacher::AttachEngine3D
  Height = 17
  Length = 2.5
  Placement = pos=(51.134,-12,-15.5) rot=(0,1,0;0.523599rad)
  Width = 2
FEATURE [Part::Box] Box007  label="Cube007"
  AttacherType = Attacher::AttachEngine3D
  Height = 9
  Length = 2.5
  Placement = pos=(59.4048,-12,-1.40558) rot=(0,1,0;0.296706rad)
  Width = 2
FEATURE [Part::Box] Box008  label="Cube008"
  AttacherType = Attacher::AttachEngine3D
  Height = 8
  Length = 2
  Placement = pos=(53.299,-12,-16.75) rot=(0,1,0;4.18879rad)
  Width = 2
FEATURE [Part::MultiFuse] Fusion001
  Placement = pos=(0,-12,0) rot=(0,0,1;0rad)
  Shapes = -> [Box006,Box007,Box008]
FEATURE [Part::Box] Box009  label="Cube009"
  AttacherType = Attacher::AttachEngine3D
  Height = 17
  Length = 2.5
  Placement = pos=(51.134,-12,-15.5) rot=(0,1,0;0.523599rad)
  Width = 2
FEATURE [Part::Box] Box010  label="Cube010"
  AttacherType = Attacher::AttachEngine3D
  Height = 9
  Length = 2.5
  Placement = pos=(59.4048,-12,-1.40558) rot=(0,1,0;0.296706rad)
  Width = 2
FEATURE [Part::Box] Box011  label="Cube011"
  AttacherType = Attacher::AttachEngine3D
  Height = 8
  Length = 2
  Placement = pos=(53.299,-12,-16.75) rot=(0,1,0;4.18879rad)
  Width = 2
FEATURE [Part::MultiFuse] Fusion002
  Placement = pos=(0,22,0) rot=(0,0,1;0rad)
  Shapes = -> [Box009,Box010,Box011]
FEATURE [Part::Box] Box012  label="Cube012"
  AttacherType = Attacher::AttachEngine3D
  Height = 17
  Length = 2.5
  Placement = pos=(51.134,-12,-15.5) rot=(0,1,0;0.523599rad)
  Width = 2
FEATURE [Part::Box] Box013  label="Cube013"
  AttacherType = Attacher::AttachEngine3D
  Height = 9
  Length = 2.5
  Placement = pos=(59.4048,-12,-1.40558) rot=(0,1,0;0.296706rad)
  Width = 2
FEATURE [Part::Box] Box014  label="Cube014"
  AttacherType = Attacher::AttachEngine3D
  Height = 8
  Length = 2
  Placement = pos=(53.299,-12,-16.75) rot=(0,1,0;4.18879rad)
  Width = 2
FEATURE [Part::MultiFuse] Fusion003
  Placement = pos=(0,34,0) rot=(0,0,1;0rad)
  Shapes = -> [Box012,Box013,Box014]
FEATURE [Sketcher::SketchObject] Sketch027
  FullyConstrained = true
  MapMode = 5
  Support = -> [XY_Plane005]
  sketch-geometry (1):
    g0: Circle CenterX=0 CenterY=0 CenterZ=0 NormalX=0 NormalY=0 NormalZ=1 AngleXU=0 Radius=7.5
  constraints (2):
    c: Coincident(g0,g-1)
    c: Diameter(g0) = 15
FEATURE [PartDesign::Pad] Pad021
  Direction = (1,1,1)
  Length = 0.2
  Length2 = 100
  Profile = -> Sketch027
  Type = 0
FEATURE [Sketcher::SketchObject] Sketch028
  FullyConstrained = true
  MapMode = 5
  Placement = pos=(0,0,0.2) rot=(0,0,1;0rad)
  Support = -> [Pad021]
  sketch-geometry (2):
    g0: Circle CenterX=0 CenterY=0 CenterZ=0 NormalX=0 NormalY=0 NormalZ=1 AngleXU=0 Radius=1.9
    g1: Circle CenterX=0 CenterY=0 CenterZ=0 NormalX=0 NormalY=0 NormalZ=1 AngleXU=0 Radius=1.45
  constraints (4):
    c: Coincident(g0,g-1)
    c: Coincident(g1,g0)
    c: Diameter(g0) = 3.8
    c: Diameter(g1) = 2.9
FEATURE [PartDesign::Pad] Pad022
  BaseFeature = -> Pad021
  Direction = (1,1,1)
  Length = 16
  Length2 = 100
  Profile = -> Sketch028
  Type = 0
FEATURE [PartDesign::Pocket] Pocket020
  BaseFeature = -> Pad022
  Direction = (1,1,1)
  Length = 5
  Length2 = 100
  Profile = -> Pad022 [Face7]
  Type = 0
FEATURE [PartDesign::Body] Body005  label="spacer_Front_Suspention"
  Group = -> [Sketch027,Pad021,Sketch028,Pad022,Pocket020]
  Origin = -> Origin005
  Tip = -> Pocket020
FEATURE [Sketcher::SketchObject] Sketch029
  FullyConstrained = true
  MapMode = 5
  Support = -> [XY_Plane006]
  sketch-geometry (7):
    g0: ArcOfCircle CenterX=0 CenterY=0 CenterZ=0 NormalX=0 NormalY=0 NormalZ=1 AngleXU=0 Radius=5 StartAngle=1.5708 EndAngle=4.71239
    g1: ArcOfCircle CenterX=24 CenterY=0 CenterZ=0 NormalX=0 NormalY=0 NormalZ=1 AngleXU=0 Radius=5 StartAngle=4.71239 EndAngle=7.85398
    g2: LineSegment StartX=-9e-16 StartY=-5 StartZ=0 EndX=24 EndY=-5 EndZ=0
    g3: LineSegment StartX=-8e-16 StartY=5 StartZ=0 EndX=24 EndY=5 EndZ=0
    g4: LineSegment StartX=-5 StartY=-7e-16 StartZ=0 EndX=29 EndY=-7e-16 EndZ=0
    g5: Circle CenterX=0 CenterY=0 CenterZ=0 NormalX=0 NormalY=0 NormalZ=1 AngleXU=0 Radius=1.6
    g6: Circle CenterX=24 CenterY=0 CenterZ=0 NormalX=0 NormalY=0 NormalZ=1 AngleXU=0 Radius=1.6
  constraints (16):
    c: Tangent(g0,g3) = 1.5708
    c: Tangent(g0,g2) = -1.5708
    c: Tangent(g2,g1) = -1.5708
    c: Tangent(g3,g1) = 1.5708
    c: Horizontal(g2)
    c: Equal(g0,g1)
    c: Coincident(g0,g-1)
    c: Distance(g0,g0) = 10
    c: PointOnObject(g4,g0)
    c: Horizontal(g4)
    c: Perpendicular(g4,g1) = 1.5708
    c: Distance(g4) = 34
    c: Coincident(g5,g0)
    c: Coincident(g6,g1)
    c: Equal(g5,g6)
    c: Diameter(g6) = 3.2
FEATURE [PartDesign::Pad] Pad023
  Direction = (1,1,1)
  Length = 11
  Length2 = 100
  Profile = -> Sketch029
  Type = 0
FEATURE [Sketcher::SketchObject] Sketch031
  ExternalGeometry = -> [Pad023]
  FullyConstrained = true
  MapMode = 5
  Placement = pos=(0,0,11) rot=(0,0,1;0rad)
  Support = -> [Pad023]
  sketch-geometry (8):
    g0: ArcOfCircle CenterX=0 CenterY=0 CenterZ=0 NormalX=0 NormalY=0 NormalZ=1 AngleXU=0 Radius=4 StartAngle=5.60805 EndAngle=6.95832
    g1: ArcOfCircle CenterX=24 CenterY=0 CenterZ=0 NormalX=0 NormalY=0 NormalZ=1 AngleXU=0 Radius=4 StartAngle=2.46646 EndAngle=3.81672
    g2: LineSegment StartX=3.1225 StartY=2.5 StartZ=0 EndX=10.5 EndY=2.5 EndZ=0
    g3: LineSegment StartX=10.5 StartY=2.5 StartZ=0 EndX=10.5 EndY=-2.5 EndZ=0
    g4: LineSegment StartX=10.5 StartY=-2.5 StartZ=0 EndX=3.1225 EndY=-2.5 EndZ=0
    g5: LineSegment StartX=20.8775 StartY=-2.5 StartZ=0 EndX=13.5 EndY=-2.5 EndZ=0
    g6: LineSegment StartX=13.5 StartY=-2.5 StartZ=0 EndX=13.5 EndY=2.5 EndZ=0
    g7: LineSegment StartX=13.5 StartY=2.5 StartZ=0 EndX=20.8775 EndY=2.5 EndZ=0
  constraints (24):
    c: Coincident(g0,g-1)
    c: Coincident(g1,g-5)
    c: Diameter(g1) = 8
    c: Diameter(g0) = 8
    c: Horizontal(g2)
    c: Coincident(g3,g2)
    c: Vertical(g3)
    c: Coincident(g4,g3)
    c: Horizontal(g4)
    c: Horizontal(g5)
    c: Coincident(g6,g5)
    c: Vertical(g6)
    c: Horizontal(g7)
    c: Coincident(g7,g6)
    c: Distance(g3,g-4) = 2.5
    c: Distance(g2,g-3) = 2.5
    c: Distance(g6,g-3) = 2.5
    c: Distance(g5,g-4) = 2.5
    c: Equal(g2,g7)
    c: Distance(g2,g6) = 3
    c: Coincident(g0,g4)
    c: Coincident(g0,g2)
    c: Coincident(g1,g7)
    c: Coincident(g1,g5)
FEATURE [Sketcher::SketchObject] Sketch032
  ExternalGeometry = -> [Pad023]
  FullyConstrained = true
  MapMode = 5
  Placement = pos=(0,0,0) rot=(1,0,0;3.14159rad)
  Support = -> [Pad023]
  sketch-geometry (8):
    g0: LineSegment StartX=3.1225 StartY=-2.5 StartZ=0 EndX=10.5 EndY=-2.5 EndZ=0
    g1: LineSegment StartX=10.5 StartY=-2.5 StartZ=0 EndX=10.5 EndY=2.5 EndZ=0
    g2: LineSegment StartX=10.5 StartY=2.5 StartZ=0 EndX=3.1225 EndY=2.5 EndZ=0
    g3: LineSegment StartX=20.8775 StartY=2.5 StartZ=0 EndX=13.5 EndY=2.5 EndZ=0
    g4: LineSegment StartX=13.5 StartY=2.5 StartZ=0 EndX=13.5 EndY=-2.5 EndZ=0
    g5: LineSegment StartX=13.5 StartY=-2.5 StartZ=0 EndX=20.8775 EndY=-2.5 EndZ=0
    g6: ArcOfCircle CenterX=24 CenterY=0 CenterZ=0 NormalX=0 NormalY=0 NormalZ=1 AngleXU=0 Radius=4 StartAngle=2.46646 EndAngle=3.81672
    g7: ArcOfCircle CenterX=0 CenterY=0 CenterZ=0 NormalX=0 NormalY=0 NormalZ=1 AngleXU=0 Radius=4 StartAngle=5.60805 EndAngle=6.95832
  constraints (24):
    c: Horizontal(g0)
    c: Coincident(g1,g0)
    c: Vertical(g1)
    c: Coincident(g2,g1)
    c: Horizontal(g2)
    c: Horizontal(g3)
    c: Coincident(g4,g3)
    c: Vertical(g4)
    c: Horizontal(g5)
    c: Coincident(g5,g4)
    c: Distance(g1,g-4) = 2.5
    c: Distance(g0,g-3) = 2.5
    c: Distance(g4,g-3) = 2.5
    c: Distance(g3,g-4) = 2.5
    c: Equal(g0,g5)
    c: Distance(g0,g4) = 3
    c: Coincident(g6,g-5)
    c: Coincident(g7,g-1)
    c: Diameter(g7) = 8
    c: Diameter(g6) = 8
    c: Coincident(g7,g0)
    c: Coincident(g7,g2)
    c: Coincident(g6,g3)
    c: Coincident(g6,g5)
FEATURE [PartDesign::Pocket] Pocket021
  BaseFeature = -> Pad023
  Direction = (1,1,1)
  Length = 3
  Length2 = 100
  Profile = -> Sketch031
  Type = 0
FEATURE [PartDesign::Pocket] Pocket022
  BaseFeature = -> Pocket021
  Direction = (1,1,1)
  Length = 3
  Length2 = 100
  Profile = -> Sketch032
  Type = 0
FEATURE [Sketcher::SketchObject] Sketch034
  AttachmentOffset = pos=(0,0,-3) rot=(0,0,1;0rad)
  ExternalGeometry = -> [Pocket022]
  FullyConstrained = true
  MapMode = 5
  Placement = pos=(0,0,8) rot=(0,0,1;0rad)
  Support = -> [Pocket022]
  sketch-geometry (8):
    g0: ArcOfCircle CenterX=-1.4 CenterY=11 CenterZ=0 NormalX=0 NormalY=0 NormalZ=1 AngleXU=0 Radius=3 StartAngle=0.569146 EndAngle=3.08683
    g1: LineSegment StartX=-4.9925 StartY=0.273681 StartZ=0 EndX=-4.3955 EndY=11.1642 EndZ=0
    g2: LineSegment StartX=-1.4 StartY=11 StartZ=0 EndX=-1.4 EndY=-5 EndZ=0
    g3: LineSegment StartX=1.12708 StartY=12.6167 StartZ=0 EndX=6 EndY=5 EndZ=0
    g4: LineSegment StartX=1.6 StartY=8.73236e-09 StartZ=0 EndX=1.6 EndY=11 EndZ=0
    g5: ArcOfCircle CenterX=0 CenterY=0 CenterZ=0 NormalX=0 NormalY=0 NormalZ=1 AngleXU=0 Radius=5 StartAngle=1.5708 EndAngle=3.08683
    g6: LineSegment StartX=-8e-16 StartY=5 StartZ=0 EndX=6 EndY=5 EndZ=0
    g7: Circle CenterX=-1.4 CenterY=11 CenterZ=0 NormalX=0 NormalY=0 NormalZ=1 AngleXU=0 Radius=3
  constraints (22):
    c: Diameter(g0) = 6
    c: Tangent(g1,g-3)
    c: Coincident(g2,g0)
    c: Vertical(g2)
    c: Horizontal(g2,g-3)
    c: Distance(g2) = 16
    c: PointOnObject(g3,g-4)
    c: PointOnObject(g4,g-5)
    c: Tangent(g4,g-5)
    c: Vertical(g4)
    c: Coincident(g5,g-1)
    c: Coincident(g5,g1)
    c: Coincident(g6,g-4)
    c: Coincident(g6,g3)
    c: Tangent(g5,g6) = 1.5708
    c: Distance(g6) = 6
    c: Tangent(g0,g1) = 1.5708
    c: Tangent(g0,g3) = 1.5708
    c: Coincident(g7,g0)
    c: Equal(g7,g0)
    c: Tangent(g4,g7)
    c: PointOnObject(g4,g7)
FEATURE [PartDesign::Pad] Pad025
  BaseFeature = -> Pocket022
  Direction = (1,1,1)
  Length = 5
  Length2 = 100
  Profile = -> Sketch034
  Reversed = true
  Type = 0
FEATURE [Sketcher::SketchObject] Sketch037
  FullyConstrained = true
  MapMode = 5
  Support = -> [XY_Plane007]
  sketch-geometry (7):
    g0: ArcOfCircle CenterX=0 CenterY=0 CenterZ=0 NormalX=0 NormalY=0 NormalZ=1 AngleXU=0 Radius=5 StartAngle=1.5708 EndAngle=4.71239
    g1: ArcOfCircle CenterX=30 CenterY=-1.54e-14 CenterZ=0 NormalX=0 NormalY=0 NormalZ=1 AngleXU=0 Radius=5 StartAngle=4.71239 EndAngle=7.85398
    g2: LineSegment StartX=-7e-16 StartY=-5 StartZ=0 EndX=30 EndY=-5 EndZ=0
    g3: LineSegment StartX=5.14e-14 StartY=5 StartZ=0 EndX=30 EndY=5 EndZ=0
    g4: LineSegment StartX=-5 StartY=-1.74e-14 StartZ=0 EndX=35 EndY=-1.74e-14 EndZ=0
    g5: Circle CenterX=0 CenterY=0 CenterZ=0 NormalX=0 NormalY=0 NormalZ=1 AngleXU=0 Radius=1.6
    g6: Circle CenterX=30 CenterY=-1.54e-14 CenterZ=0 NormalX=0 NormalY=0 NormalZ=1 AngleXU=0 Radius=1.6
  constraints (16):
    c: Tangent(g0,g3) = 1.5708
    c: Tangent(g0,g2) = -1.5708
    c: Tangent(g2,g1) = -1.5708
    c: Tangent(g3,g1) = 1.5708
    c: Horizontal(g2)
    c: Equal(g0,g1)
    c: Coincident(g0,g-1)
    c: Distance(g0,g0) = 10
    c: PointOnObject(g4,g0)
    c: Horizontal(g4)
    c: Perpendicular(g4,g1) = 1.5708
    c: Distance(g4) = 40
    c: Coincident(g5,g0)
    c: Coincident(g6,g1)
    c: Equal(g5,g6)
    c: Diameter(g6) = 3.2
FEATURE [PartDesign::Pad] Pad026
  Direction = (1,1,1)
  Length = 11
  Length2 = 100
  Profile = -> Sketch037
  Type = 0
FEATURE [Sketcher::SketchObject] Sketch035
  ExternalGeometry = -> [Pad026]
  FullyConstrained = true
  MapMode = 5
  Placement = pos=(0,0,11) rot=(0,0,1;0rad)
  Support = -> [Pad026]
  sketch-geometry (8):
    g0: ArcOfCircle CenterX=0 CenterY=0 CenterZ=0 NormalX=0 NormalY=0 NormalZ=1 AngleXU=0 Radius=4 StartAngle=5.60805 EndAngle=6.95832
    g1: ArcOfCircle CenterX=30 CenterY=-1.54e-14 CenterZ=0 NormalX=0 NormalY=0 NormalZ=1 AngleXU=0 Radius=4 StartAngle=2.46646 EndAngle=3.81672
    g2: LineSegment StartX=3.1225 StartY=2.5 StartZ=0 EndX=13.5 EndY=2.5 EndZ=0
    g3: LineSegment StartX=13.5 StartY=2.5 StartZ=0 EndX=13.5 EndY=-2.5 EndZ=0
    g4: LineSegment StartX=13.5 StartY=-2.5 StartZ=0 EndX=3.1225 EndY=-2.5 EndZ=0
    g5: LineSegment StartX=26.8775 StartY=-2.5 StartZ=0 EndX=16.5 EndY=-2.5 EndZ=0
    g6: LineSegment StartX=16.5 StartY=-2.5 StartZ=0 EndX=16.5 EndY=2.5 EndZ=0
    g7: LineSegment StartX=16.5 StartY=2.5 StartZ=0 EndX=26.8775 EndY=2.5 EndZ=0
  constraints (24):
    c: Coincident(g0,g-1)
    c: Coincident(g1,g-5)
    c: Diameter(g1) = 8
    c: Diameter(g0) = 8
    c: Horizontal(g2)
    c: Coincident(g3,g2)
    c: Vertical(g3)
    c: Coincident(g4,g3)
    c: Horizontal(g4)
    c: Horizontal(g5)
    c: Coincident(g6,g5)
    c: Vertical(g6)
    c: Horizontal(g7)
    c: Coincident(g7,g6)
    c: Distance(g3,g-4) = 2.5
    c: Distance(g2,g-3) = 2.5
    c: Distance(g6,g-3) = 2.5
    c: Distance(g5,g-4) = 2.5
    c: Equal(g2,g7)
    c: Distance(g2,g6) = 3
    c: Coincident(g0,g4)
    c: Coincident(g0,g2)
    c: Coincident(g1,g7)
    c: Coincident(g1,g5)
FEATURE [Sketcher::SketchObject] Sketch036
  ExternalGeometry = -> [Pad026]
  FullyConstrained = true
  MapMode = 5
  Placement = pos=(0,0,0) rot=(1,0,0;3.14159rad)
  Support = -> [Pad026]
  sketch-geometry (8):
    g0: LineSegment StartX=3.1225 StartY=-2.5 StartZ=0 EndX=13.5 EndY=-2.5 EndZ=0
    g1: LineSegment StartX=13.5 StartY=-2.5 StartZ=0 EndX=13.5 EndY=2.5 EndZ=0
    g2: LineSegment StartX=13.5 StartY=2.5 StartZ=0 EndX=3.1225 EndY=2.5 EndZ=0
    g3: LineSegment StartX=26.8775 StartY=2.5 StartZ=0 EndX=16.5 EndY=2.5 EndZ=0
    g4: LineSegment StartX=16.5 StartY=2.5 StartZ=0 EndX=16.5 EndY=-2.5 EndZ=0
    g5: LineSegment StartX=16.5 StartY=-2.5 StartZ=0 EndX=26.8775 EndY=-2.5 EndZ=0
    g6: ArcOfCircle CenterX=30 CenterY=1.54e-14 CenterZ=0 NormalX=0 NormalY=0 NormalZ=1 AngleXU=0 Radius=4 StartAngle=2.46646 EndAngle=3.81672
    g7: ArcOfCircle CenterX=0 CenterY=0 CenterZ=0 NormalX=0 NormalY=0 NormalZ=1 AngleXU=0 Radius=4 StartAngle=5.60805 EndAngle=6.95832
  constraints (24):
    c: Horizontal(g0)
    c: Coincident(g1,g0)
    c: Vertical(g1)
    c: Coincident(g2,g1)
    c: Horizontal(g2)
    c: Horizontal(g3)
    c: Coincident(g4,g3)
    c: Vertical(g4)
    c: Horizontal(g5)
    c: Coincident(g5,g4)
    c: Distance(g1,g-4) = 2.5
    c: Distance(g0,g-3) = 2.5
    c: Distance(g4,g-3) = 2.5
    c: Distance(g3,g-4) = 2.5
    c: Equal(g0,g5)
    c: Distance(g0,g4) = 3
    c: Coincident(g6,g-5)
    c: Coincident(g7,g-1)
    c: Diameter(g7) = 8
    c: Diameter(g6) = 8
    c: Coincident(g7,g0)
    c: Coincident(g7,g2)
    c: Coincident(g6,g3)
    c: Coincident(g6,g5)
FEATURE [PartDesign::Pocket] Pocket023
  BaseFeature = -> Pad026
  Direction = (1,1,1)
  Length = 3
  Length2 = 100
  Profile = -> Sketch035
  Type = 0
FEATURE [PartDesign::Pocket] Pocket024
  BaseFeature = -> Pocket023
  Direction = (1,1,1)
  Length = 3
  Length2 = 100
  Profile = -> Sketch036
  Type = 0
FEATURE [PartDesign::Fillet] Fillet011
  Base = -> Pad025 [Edge58,Edge60,Edge49,Edge50,Edge62,Edge57,Edge52,Edge54]
  BaseFeature = -> Pad025
  Radius = 1
  SupportTransform = false
  UseAllEdges = false
FEATURE [PartDesign::Fillet] Fillet012
  Base = -> Fillet011 [Edge95,Edge93,Edge99,Edge98,Edge101,Edge91,Edge103,Edge90]
  BaseFeature = -> Fillet011
  Radius = 1
  SupportTransform = false
  UseAllEdges = false
FEATURE [Sketcher::SketchObject] Sketch038
  AttachmentOffset = pos=(0,0,-3) rot=(0,0,1;0rad)
  ExternalGeometry = -> [Pocket024]
  FullyConstrained = true
  MapMode = 5
  Placement = pos=(0,0,8) rot=(0,0,1;0rad)
  Support = -> [Pocket024]
  sketch-geometry (9):
    g0: Circle CenterX=1 CenterY=11.25 CenterZ=0 NormalX=0 NormalY=0 NormalZ=1 AngleXU=0 Radius=3.75
    g1: LineSegment StartX=-4.79048 StartY=1.43225 StartZ=0 EndX=-2.35565 EndY=9.57606 EndZ=0
    g2: LineSegment StartX=4.68453 StartY=11.9476 StartZ=0 EndX=6 EndY=5 EndZ=0
    g3: LineSegment StartX=1 StartY=15 StartZ=0 EndX=1 EndY=-5 EndZ=0
    g4: ArcOfCircle CenterX=1 CenterY=11.25 CenterZ=0 NormalX=0 NormalY=0 NormalZ=1 AngleXU=0 Radius=3.75 StartAngle=0.18713 EndAngle=3.60431
    g5: LineSegment StartX=4.68453 StartY=11.9476 StartZ=0 EndX=6 EndY=5 EndZ=0
    g6: LineSegment StartX=6 StartY=5 StartZ=0 EndX=5.15e-14 EndY=5 EndZ=0
    g7: LineSegment StartX=-4.79048 StartY=1.43225 StartZ=0 EndX=-2.35565 EndY=9.57606 EndZ=0
    g8: ArcOfCircle CenterX=0 CenterY=0 CenterZ=0 NormalX=0 NormalY=0 NormalZ=1 AngleXU=0 Radius=5 StartAngle=1.5708 EndAngle=2.85107
  constraints (26):
    c: PointOnObject(g1,g0)
    c: Tangent(g1,g-3)
    c: Diameter(g0) = 7.5
    c: PointOnObject(g2,g0)
    c: PointOnObject(g2,g-4)
    c: Tangent(g2,g0)
    c: PointOnObject(g3,g0)
    c: Vertical(g3)
    c: Horizontal(g3,g-3)
    c: Perpendicular(g0,g3)
    c: Distance(g3) = 20
    c: DistanceX(g-2,g0) = 1
    c: Distance(g2,g-4) = 6
    c: Distance(g1) = 8.5
    c: Coincident(g4,g0)
    c: Coincident(g4,g1)
    c: Coincident(g5,g4)
    c: Coincident(g5,g2)
    c: Coincident(g6,g5)
    c: Coincident(g6,g-4)
    c: Coincident(g7,g1)
    c: Coincident(g7,g4)
    c: Coincident(g8,g-1)
    c: Coincident(g8,g7)
    c: Coincident(g8,g6)
    c: Equal(g2,g5)
FEATURE [PartDesign::Pad] Pad027
  BaseFeature = -> Pocket024
  Direction = (1,1,1)
  Length = 5
  Length2 = 100
  Profile = -> Sketch038
  Reversed = true
  Type = 0
FEATURE [PartDesign::Fillet] Fillet013
  Base = -> Pad027 [Edge73,Edge70,Edge66,Edge76,Edge78,Edge65,Edge68,Edge74,Edge58,Edge52,Edge57,Edge50,Edge48,Edge62,Edge60,Edge47]
  BaseFeature = -> Pad027
  Radius = 1
  SupportTransform = false
  UseAllEdges = false
FEATURE [PartDesign::Fillet] Fillet014
  Base = -> Fillet013 [Edge49]
  BaseFeature = -> Fillet013
  Radius = 1
  SupportTransform = false
  UseAllEdges = false
FEATURE [PartDesign::Body] Body007  label="Suspension_Long"
  Group = -> [Sketch037,Pad026,Sketch035,Pocket023,Sketch036,Pocket024,Sketch038,Pad027,Fillet013,Fillet014]
  Origin = -> Origin007
  Tip = -> Fillet014
FEATURE [PartDesign::Fillet] Fillet015
  Base = -> Fillet012 [Edge49]
  BaseFeature = -> Fillet012
  Radius = 1
  SupportTransform = false
  UseAllEdges = false
FEATURE [PartDesign::Body] Body006  label="Suspension_Short"
  Group = -> [Sketch029,Pad023,Sketch031,Pocket021,Sketch032,Pocket022,Sketch034,Pad025,Fillet011,Fillet012,Fillet015]
  Origin = -> Origin006
  Placement = pos=(0,0,-23) rot=(0,0,1;0rad)
  Tip = -> Fillet015
FEATURE [Mesh::Feature] Tamiya_Neo_Fighter_DT_03_Servo_Saver  label="Tamiya_Neo_Fighter_DT-03_Servo_Saver"
FEATURE [Part::Feature] Tamiya_Neo_Fighter_DT_03_Servo_Saver001
  shape: bbox 15.5 x 27.75 x 9.32 mm, 8374 faces, 0 solids (baked)
FEATURE [Part::Feature] Tamiya_Neo_Fighter_DT_03_Servo_Saver001_solid  label="Tamiya_Neo_Fighter_DT_03_Servo_Saver001 (Solid)"
  shape: bbox 15.5 x 27.75 x 9.32 mm, 8374 faces (baked)
FEATURE [Part::FeaturePython] Tube  # WARN: FeaturePython — macro-defined, semantics opaque (R4)
  AttacherType = Attacher::AttachEngine3D
  Height = 5
  InnerRadius = 1
  OuterRadius = 3
  Placement = pos=(-4.4,-16.65,7.3) rot=(0,0,1;0rad)
FEATURE [Part::FeaturePython] Tube001  # WARN: FeaturePython — macro-defined, semantics opaque (R4)
  AttacherType = Attacher::AttachEngine3D
  Height = 5
  InnerRadius = 1
  OuterRadius = 3
  Placement = pos=(4.4,-16.65,7.3) rot=(0,0,1;0rad)
FEATURE [Part::MultiFuse] Fusion004
  Shapes = -> [Tamiya_Neo_Fighter_DT_03_Servo_Saver001_solid,Tube,Tube001]
FEATURE [PartDesign::FeatureBase] BaseFeature001
  BaseFeature = -> Fusion004
FEATURE [PartDesign::Body] Body008  label="ServoSaver"
  BaseFeature = -> Fusion004
  Group = -> [BaseFeature001]
  Origin = -> Origin008
  Tip = -> BaseFeature001
FEATURE [Sketcher::SketchObject] Sketch039
  FullyConstrained = true
  MapMode = 5
  Support = -> [XY_Plane009]
  sketch-geometry (5):
    g0: ArcOfCircle CenterX=0 CenterY=0 CenterZ=0 NormalX=0 NormalY=0 NormalZ=1 AngleXU=0 Radius=8 StartAngle=1.5708 EndAngle=4.71239
    g1: ArcOfCircle CenterX=1.75 CenterY=0 CenterZ=0 NormalX=0 NormalY=0 NormalZ=1 AngleXU=0 Radius=9.75 StartAngle=5.32088 EndAngle=7.24549
    g2: LineSegment StartX=-1.3e-15 StartY=8 StartZ=0 EndX=7.32337 EndY=8 EndZ=0
    g3: LineSegment StartX=-1.5e-15 StartY=-8 StartZ=0 EndX=7.32337 EndY=-8 EndZ=0
    g4: LineSegment StartX=-8 StartY=-6e-16 StartZ=0 EndX=11.5 EndY=-6e-16 EndZ=0
  constraints (14):
    c: Coincident(g0,g-1)
    c: Diameter(g0) = 16
    c: PointOnObject(g1,g-1)
    c: Diameter(g1) = 19.5
    c: PointOnObject(g4,g0)
    c: Horizontal(g4)
    c: Perpendicular(g4,g1) = 1.5708
    c: Distance(g4) = 19.5
    c: Horizontal(g2)
    c: Horizontal(g3)
    c: Coincident(g1,g2)
    c: Coincident(g1,g3)
    c: Tangent(g0,g2) = 1.5708
    c: Tangent(g0,g3) = -1.5708
FEATURE [PartDesign::Pad] Pad028
  Direction = (1,1,1)
  Length = 3
  Length2 = 100
  Profile = -> Sketch039
  Type = 0
FEATURE [Sketcher::SketchObject] Sketch040
  ExternalGeometry = -> [Pad028]
  FullyConstrained = true
  MapMode = 5
  Placement = pos=(0,0,3) rot=(0,0,1;0rad)
  Support = -> [Pad028]
  sketch-geometry (4):
    g0: ArcOfCircle CenterX=-0.25 CenterY=0 CenterZ=0 NormalX=0 NormalY=0 NormalZ=1 AngleXU=0 Radius=9.75 StartAngle=5.32088 EndAngle=7.24549
    g1: LineSegment StartX=7.32337 StartY=8 StartZ=0 EndX=5.32337 EndY=8 EndZ=0
    g2: LineSegment StartX=7.32337 StartY=-8 StartZ=0 EndX=5.32337 EndY=-8 EndZ=0
    g3: ArcOfCircle CenterX=1.75 CenterY=0 CenterZ=0 NormalX=0 NormalY=0 NormalZ=1 AngleXU=0 Radius=9.75 StartAngle=5.32088 EndAngle=7.24549
  constraints (12):
    c: Equal(g-3,g0)
    c: PointOnObject(g0,g-1)
    c: Distance(g-3,g0) = 2
    c: Coincident(g1,g-4)
    c: Horizontal(g1)
    c: Coincident(g2,g-5)
    c: Horizontal(g2)
    c: Coincident(g3,g-3)
    c: Coincident(g0,g1)
    c: Coincident(g3,g1)
    c: Coincident(g0,g2)
    c: PointOnObject(g3,g2)
FEATURE [PartDesign::Pad] Pad029
  BaseFeature = -> Pad028
  Direction = (1,1,1)
  Length = 7.4
  Length2 = 100
  Profile = -> Sketch040
  Type = 0
FEATURE [Sketcher::SketchObject] Sketch041
  ExternalGeometry = -> [Pad029]
  FullyConstrained = false
  MapMode = 5
  Placement = pos=(0,0,3) rot=(0,0,1;0rad)
  Support = -> [Pad029]
  sketch-geometry (6):
    g0: ArcOfCircle CenterX=0 CenterY=0 CenterZ=0 NormalX=0 NormalY=0 NormalZ=1 AngleXU=0 Radius=5.75 StartAngle=3.51546 EndAngle=9.05091
    g1: Circle CenterX=0 CenterY=0 CenterZ=0 NormalX=0 NormalY=0 NormalZ=1 AngleXU=0 Radius=3.75
    g2: LineSegment StartX=-5.3528 StartY=2.1 StartZ=0 EndX=-7.71946 EndY=2.1 EndZ=0
    g3: LineSegment StartX=-7.71946 StartY=-2.1 StartZ=0 EndX=-5.3528 EndY=-2.1 EndZ=0
    g4: ArcOfCircle CenterX=0 CenterY=0 CenterZ=0 NormalX=0 NormalY=0 NormalZ=1 AngleXU=0 Radius=8 StartAngle=2.87598 EndAngle=3.4072
    g5: LineSegment StartX=2.95195 StartY=2.31268 StartZ=0 EndX=4.52632 EndY=3.54611 EndZ=0
  constraints (18):
    c: Coincident(g0,g-1)
    c: Coincident(g1,g0)
    c: Diameter(g0) = 11.5
    c: Diameter(g1) = 7.5
    c: Horizontal(g2)
    c: Horizontal(g3)
    c: Coincident(g2,g0)
    c: Coincident(g0,g3)
    c: Vertical(g0,g0)
    c: Coincident(g4,g0)
    c: Equal(g4,g-3)
    c: Coincident(g4,g2)
    c: Coincident(g4,g3)
    c: Distance(g0,g0) = 4.2
    c: PointOnObject(g5,g1)
    c: PointOnObject(g5,g0)
    c: Perpendicular(g0,g5)
    c: Distance(g5) = 2
FEATURE [PartDesign::Pad] Pad030
  BaseFeature = -> Pad029
  Direction = (1,1,1)
  Length = 4.2
  Length2 = 100
  Profile = -> Sketch041
  Type = 0
FEATURE [PartDesign::Pocket] Pocket025
  BaseFeature = -> Pad030
  Direction = (1,1,1)
  Length = 5
  Length2 = 100
  Profile = -> Pad030 [Face18]
  Type = 0
FEATURE [Sketcher::SketchObject] Sketch042
  ExternalGeometry = -> [Pocket025]
  FullyConstrained = true
  MapMode = 5
  Placement = pos=(0,0,7.2) rot=(0,0,1;0rad)
  Support = -> [Pocket025]
  sketch-geometry (2):
    g0: Circle CenterX=0 CenterY=0 CenterZ=0 NormalX=0 NormalY=0 NormalZ=1 AngleXU=0 Radius=3.75
    g1: Circle CenterX=0 CenterY=0 CenterZ=0 NormalX=0 NormalY=0 NormalZ=1 AngleXU=0 Radius=3.1
  constraints (5):
    c: Coincident(g0,g-1)
    c: Equal(g0,g-3)
    c: Coincident(g1,g0)
    c: Diameter(g1) = 6.2
    c: Diameter(g0) = 7.5
FEATURE [PartDesign::Pad] Pad031
  BaseFeature = -> Pocket025
  Direction = (1,1,1)
  Length = 2.1
  Length2 = 100
  Profile = -> Sketch042
  Refine = true
  Reversed = true
  Type = 0
FEATURE [Sketcher::SketchObject] Sketch043
  ExternalGeometry = -> [Pad031]
  FullyConstrained = false
  MapMode = 5
  Placement = pos=(0,0,10.4) rot=(0,0,1;0rad)
  Support = -> [Pad031]
  sketch-geometry (15):
    g0: LineSegment StartX=7.32337 StartY=8 StartZ=0 EndX=19.5 EndY=8 EndZ=0
    g1: LineSegment StartX=21.5 StartY=6 StartZ=0 EndX=21.5 EndY=-6 EndZ=0
    g2: LineSegment StartX=22.5 StartY=0 StartZ=0 EndX=22.5 EndY=6 EndZ=0
    g3: LineSegment StartX=22.5 StartY=0 StartZ=0 EndX=22.5 EndY=-6 EndZ=0
    g4: ArcOfCircle CenterX=19.5 CenterY=6 CenterZ=0 NormalX=0 NormalY=0 NormalZ=1 AngleXU=0 Radius=2 StartAngle=0 EndAngle=1.5708
    g5: LineSegment StartX=0 StartY=1.72262 StartZ=0 EndX=21.5 EndY=1.72262 EndZ=0
    g6: LineSegment StartX=7.32337 StartY=-8 StartZ=0 EndX=19.5 EndY=-8 EndZ=0
    g7: ArcOfCircle CenterX=19.5 CenterY=-6 CenterZ=0 NormalX=0 NormalY=0 NormalZ=1 AngleXU=0 Radius=2 StartAngle=4.71239 EndAngle=6.28319
    g8: ArcOfCircle CenterX=1.75 CenterY=0 CenterZ=0 NormalX=0 NormalY=0 NormalZ=1 AngleXU=0 Radius=9.75 StartAngle=5.32088 EndAngle=7.24549
    g9: Circle CenterX=18 CenterY=4.5 CenterZ=0 NormalX=0 NormalY=0 NormalZ=1 AngleXU=0 Radius=1.35
    g10: Circle CenterX=18 CenterY=-4.5 CenterZ=0 NormalX=0 NormalY=0 NormalZ=1 AngleXU=0 Radius=1.35
    g11: LineSegment StartX=0 StartY=9.70824 StartZ=0 EndX=18 EndY=9.70824 EndZ=0
    g12: Circle CenterX=18 CenterY=4.5 CenterZ=0 NormalX=0 NormalY=0 NormalZ=1 AngleXU=0 Radius=2.75
    g13: LineSegment StartX=18 StartY=4.5 StartZ=0 EndX=18 EndY=0 EndZ=0
    g14: LineSegment StartX=18 StartY=0 StartZ=0 EndX=18 EndY=-4.5 EndZ=0
  constraints (41):
    c: Coincident(g0,g-3)
    c: Vertical(g1)
    c: PointOnObject(g2,g-1)
    c: Vertical(g2)
    c: Coincident(g3,g2)
    c: Vertical(g3)
    c: Tangent(g1,g4) = 1.5708
    c: Tangent(g0,g4) = 1.5708
    c: Distance(g1,g4) = 2
    c: Horizontal(g1,g2)
    c: Horizontal(g3,g1)
    c: Equal(g3,g2)
    c: Distance(g2) = 6
    c: PointOnObject(g5,g-2)
    c: Horizontal(g5)
    c: PointOnObject(g5,g1)
    c: Distance(g5) = 21.5
    c: DistanceX(g5,g2) = 1
    c: Coincident(g6,g-3)
    c: Distance(g7,g1) = 2
    c: Tangent(g7,g6) = -1.5708
    c: Tangent(g7,g1) = 1.5708
    c: Coincident(g8,g-3)
    c: Coincident(g8,g0)
    c: Coincident(g8,g6)
    c: Diameter(g9) = 2.7
    c: Diameter(g10) = 2.7
    c: PointOnObject(g11,g-2)
    c: Horizontal(g11)
    c: Vertical(g11,g9)
    c: Vertical(g9,g10)
    c: Distance(g11) = 18
    c: Diameter(g12) = 5.5
    c: Distance(g9,g10) = 9
    c: Coincident(g13,g9)
    c: PointOnObject(g13,g-1)
    c: Vertical(g13)
    c: Coincident(g14,g13)
    c: Coincident(g14,g10)
    c: Equal(g14,g13)
    c: Coincident(g12,g9)
FEATURE [PartDesign::Pad] Pad032
  BaseFeature = -> Pad031
  Direction = (1,1,1)
  Length = 2.2
  Length2 = 100
  Profile = -> Sketch043
  Reversed = true
  Type = 0
FEATURE [Sketcher::SketchObject] Sketch044
  ExternalGeometry = -> [Pad032]
  FullyConstrained = true
  MapMode = 5
  Placement = pos=(0,0,10.4) rot=(0,0,1;0rad)
  Support = -> [Pad032]
  sketch-geometry (4):
    g0: Circle CenterX=18 CenterY=4.5 CenterZ=0 NormalX=0 NormalY=0 NormalZ=1 AngleXU=0 Radius=3.5
    g1: Circle CenterX=18 CenterY=4.5 CenterZ=0 NormalX=0 NormalY=0 NormalZ=1 AngleXU=0 Radius=1.35
    g2: Circle CenterX=18 CenterY=-4.5 CenterZ=0 NormalX=0 NormalY=0 NormalZ=1 AngleXU=0 Radius=3.5
    g3: Circle CenterX=18 CenterY=-4.5 CenterZ=0 NormalX=0 NormalY=0 NormalZ=1 AngleXU=0 Radius=1.35
  constraints (8):
    c: Coincident(g0,g-3)
    c: Coincident(g1,g0)
    c: Coincident(g2,g-4)
    c: Coincident(g3,g2)
    c: Equal(g3,g-4)
    c: Equal(g1,g-3)
    c: Diameter(g0) = 7
    c: Diameter(g2) = 7
FEATURE [PartDesign::Pad] Pad033
  BaseFeature = -> Pad032
  Direction = (1,1,1)
  Length = 3
  Length2 = 100
  Profile = -> Sketch044
  Refine = true
  Type = 0
FEATURE [PartDesign::Chamfer] Chamfer004
  Angle = 70
  Base = -> Pad033 [Edge36,Edge37]
  BaseFeature = -> Pad033
  ChamferType = 2
  FlipDirection = false
  Size = 0.5
  Size2 = 1
  SupportTransform = false
  UseAllEdges = false
FEATURE [PartDesign::Fillet] Fillet016
  Base = -> Chamfer004 [Edge13]
  BaseFeature = -> Chamfer004
  Radius = 1
  SupportTransform = false
  UseAllEdges = false
FEATURE [PartDesign::Fillet] Fillet017
  Base = -> Fillet016 [Edge44]
  BaseFeature = -> Fillet016
  Radius = 1
  SupportTransform = false
  UseAllEdges = false
FEATURE [PartDesign::Fillet] Fillet018
  Base = -> Fillet017 [Edge33]
  BaseFeature = -> Fillet017
  Radius = 5
  SupportTransform = false
  UseAllEdges = false
FEATURE [PartDesign::Pad] Pad034
  BaseFeature = -> Fillet018
  Direction = (1,1,1)
  Length = 3
  Length2 = 100
  Profile = -> Fillet018 [Face6]
  Type = 0
FEATURE [PartDesign::Pad] Pad035
  BaseFeature = -> Pad034
  Direction = (1,1,1)
  Length = 3
  Length2 = 100
  Profile = -> Pad034 [Face28]
  Refine = true
  Type = 0
FEATURE [PartDesign::Fillet] Fillet019
  Base = -> Pad035 [Edge24]
  BaseFeature = -> Pad035
  Radius = 1
  SupportTransform = false
  UseAllEdges = false
FEATURE [PartDesign::Body] Body009  label="ServoSaver2"
  Group = -> [Sketch039,Pad028,Sketch040,Pad029,Sketch041,Pad030,Pocket025,Sketch042,Pad031,Sketch043,Pad032,Sketch044,Pad033,Chamfer004,Fillet016,Fillet017,Fillet018,Pad034,Pad035,Fillet019]
  Origin = -> Origin009
  Tip = -> Fillet019
FEATURE [Part::FeaturePython] Tube002  # WARN: FeaturePython — macro-defined, semantics opaque (R4)
  AttacherType = Attacher::AttachEngine3D
  Height = 7
  InnerRadius = 6
  OuterRadius = 9
  Placement = pos=(0,0,2) rot=(0,0,1;0rad)
FEATURE [PartDesign::FeatureBase] BaseFeature002
  BaseFeature = -> Tube002
FEATURE [Sketcher::SketchObject] Sketch045
  ExternalGeometry = -> [BaseFeature002]
  FullyConstrained = true
  MapMode = 5
  Placement = pos=(0,0,7) rot=(0,0,1;0rad)
  Support = -> [BaseFeature002]
  sketch-geometry (4):
    g0: ArcOfCircle CenterX=0 CenterY=0 CenterZ=0 NormalX=0 NormalY=0 NormalZ=1 AngleXU=0 Radius=6 StartAngle=2.78402 EndAngle=3.49916
    g1: ArcOfCircle CenterX=0 CenterY=0 CenterZ=0 NormalX=0 NormalY=0 NormalZ=1 AngleXU=0 Radius=9 StartAngle=2.90609 EndAngle=3.3771
    g2: LineSegment StartX=-5.6205 StartY=2.1 StartZ=0 EndX=-8.75157 EndY=2.1 EndZ=0
    g3: LineSegment StartX=-5.6205 StartY=-2.1 StartZ=0 EndX=-8.75157 EndY=-2.1 EndZ=0
  constraints (12):
    c: Coincident(g0,g-1)
    c: Coincident(g1,g0)
    c: Equal(g1,g-4)
    c: Equal(g0,g-3)
    c: Horizontal(g2)
    c: Horizontal(g3)
    c: Coincident(g1,g2)
    c: Coincident(g1,g3)
    c: Coincident(g0,g2)
    c: Coincident(g0,g3)
    c: Vertical(g0,g0)
    c: DistanceY(g0,g0) = 4.2
FEATURE [PartDesign::Pocket] Pocket026
  BaseFeature = -> BaseFeature002
  Direction = (1,1,1)
  Length = 7
  Length2 = 100
  Profile = -> Sketch045
  Type = 0
FEATURE [PartDesign::Body] Body010  label="ServoSaverRing"
  BaseFeature = -> Tube002
  Group = -> [BaseFeature002,Sketch045,Pocket026]
  Origin = -> Origin010
  Placement = pos=(0,0,2) rot=(0,0,1;0rad)
  Tip = -> Pocket026
FEATURE [Mesh::Feature] X_drive_540_1  label="X-drive 540-1"
FEATURE [Part::Feature] X_drive_540_1001_solid  label="X_drive_540_1001 (Solid)"
  Placement = pos=(-0.316987,1.54904,1.5) rot=(0,0,1;3.73501rad)
  shape: bbox 35.6 x 35.6 x 70.85 mm, 5903 faces (baked)
FEATURE [Part::Feature] Blackfoot_motor_mount001_solid  label="Blackfoot_motor_mount001 (Solid)"
  Placement = pos=(-27.8205,-8.18653,53) rot=(0,0,-1;0.523599rad)
  shape: bbox 35.12 x 33.98 x 5.85 mm, 1350 faces (baked)
FEATURE [PartDesign::FeatureBase] BaseFeature003
  BaseFeature = -> Blackfoot_motor_mount001_solid
FEATURE [Sketcher::SketchObject] Sketch046
  ExternalGeometry = -> [BaseFeature003]
  FullyConstrained = true
  MapMode = 5
  Placement = pos=(0,0,5) rot=(0,0,1;0rad)
  Support = -> [BaseFeature003]
  sketch-geometry (3):
    g0: ArcOfCircle CenterX=19.2448 CenterY=21.8895 CenterZ=0 NormalX=0 NormalY=0 NormalZ=1 AngleXU=0 Radius=18 StartAngle=5.94504 EndAngle=10.0761
    g1: ArcOfCircle CenterX=19.2477 CenterY=18.0059 CenterZ=0 NormalX=0 NormalY=0 NormalZ=1 AngleXU=0 Radius=15.95 StartAngle=2.20457 EndAngle=3.59796
    g2: ArcOfCircle CenterX=20.6 CenterY=19.1191 CenterZ=0 NormalX=0 NormalY=0 NormalZ=1 AngleXU=0 Radius=15.95 StartAngle=6.08113 EndAngle=8.59763
  constraints (12):
    c: Diameter(g1) = 31.9
    c: Diameter(g0) = 36
    c: DistanceX(g0) = 19.2448
    c: DistanceY(g0) = 21.8895
    c: DistanceX(g2) = 20.6
    c: DistanceY(g2) = 19.1191
    c: DistanceX(g1) = 19.2477
    c: DistanceY(g1) = 18.0059
    c: Diameter(g2) = 31.9
    c: Coincident(g2,g1)
    c: Coincident(g1,g0)
    c: Coincident(g2,g0)
FEATURE [PartDesign::Pad] Pad036
  BaseFeature = -> BaseFeature003
  Direction = (0,0,1)
  Length = 5
  Length2 = 10
  Profile = -> Sketch046
  ReferenceAxis = -> Sketch046 [N_Axis]
  Refine = true
  Reversed = true
  Type = 0
FEATURE [Sketcher::SketchObject] Sketch047
  FullyConstrained = false
  MapMode = 5
  Placement = pos=(0,0,-1e-16) rot=(1,0,0;3.14159rad)
  Support = -> [Pad036]
  sketch-geometry (8):
    g0: LineSegment StartX=4.11234 StartY=-23.9349 StartZ=0 EndX=7.87079 EndY=-23.9349 EndZ=0
    g1: LineSegment StartX=7.87079 StartY=-23.9349 StartZ=0 EndX=7.87079 EndY=-29.2082 EndZ=0
    g2: LineSegment StartX=7.87079 StartY=-29.2082 StartZ=0 EndX=4.11234 EndY=-29.2082 EndZ=0
    g3: LineSegment StartX=4.11234 StartY=-29.2082 StartZ=0 EndX=4.11234 EndY=-23.9349 EndZ=0
    g4: LineSegment StartX=12.6652 StartY=-32.5826 StartZ=0 EndX=14.0556 EndY=-32.5826 EndZ=0
    g5: LineSegment StartX=14.0556 StartY=-32.5826 StartZ=0 EndX=14.0556 EndY=-34.2221 EndZ=0
    g6: LineSegment StartX=14.0556 StartY=-34.2221 StartZ=0 EndX=12.6652 EndY=-34.2221 EndZ=0
    g7: LineSegment StartX=12.6652 StartY=-34.2221 StartZ=0 EndX=12.6652 EndY=-32.5826 EndZ=0
  constraints (16):
    c: Coincident(g0,g1)
    c: Coincident(g1,g2)
    c: Coincident(g2,g3)
    c: Coincident(g3,g0)
    c: Horizontal(g0)
    c: Horizontal(g2)
    c: Vertical(g1)
    c: Vertical(g3)
    c: Coincident(g4,g5)
    c: Coincident(g5,g6)
    c: Coincident(g6,g7)
    c: Coincident(g7,g4)
    c: Horizontal(g4)
    c: Horizontal(g6)
    c: Vertical(g5)
    c: Vertical(g7)
FEATURE [PartDesign::Pad] Pad037
  BaseFeature = -> Pad036
  Direction = (0,0,-1)
  Length = 10
  Length2 = 10
  Profile = -> Sketch047
  ReferenceAxis = -> Sketch047 [N_Axis]
  Refine = true
  Reversed = true
  Type = 3
  UpToFace = -> Pad036 [Face122]
FEATURE [Sketcher::SketchObject] Sketch048
  ExternalGeometry = -> [Pad037]
  FullyConstrained = true
  MapMode = 5
  Placement = pos=(0,1e-16,5) rot=(0,0,1;0rad)
  Support = -> [Pad037]
  sketch-geometry (3):
    g0: LineSegment StartX=8.3156 StartY=13.5837 StartZ=0 EndX=9.24265 EndY=16.4369 EndZ=0
    g1: LineSegment StartX=8.77912 StartY=16.5103 StartZ=0 EndX=8.77912 EndY=13.5103 EndZ=0
    g2: Circle CenterX=8.77912 CenterY=15.0103 CenterZ=0 NormalX=0 NormalY=0 NormalZ=1 AngleXU=0 Radius=2.75
  constraints (7):
    c: Coincident(g0,g-3)
    c: Coincident(g0,g-4)
    c: Coincident(g1,g-4)
    c: Coincident(g1,g-3)
    c: PointOnObject(g-5,g2)
    c: PointOnObject(g2,g1)
    c: PointOnObject(g2,g0)
FEATURE [PartDesign::Pocket] Pocket027
  BaseFeature = -> Pad037
  Direction = (0,0,-1)
  Length = 0
  Length2 = 5
  Profile = -> Sketch048
  ReferenceAxis = -> Sketch048 [N_Axis]
  Type = 3
  UpToFace = -> Pad037 [Face234]
FEATURE [Sketcher::SketchObject] Sketch049
  ExternalGeometry = -> [Pocket027]
  FullyConstrained = true
  MapMode = 5
  Placement = pos=(0,1e-16,5) rot=(0,0,1;0rad)
  Support = -> [Pocket027]
  sketch-geometry (3):
    g0: LineSegment StartX=28.5389 StartY=30.3281 StartZ=0 EndX=30.3022 EndY=27.9011 EndZ=0
    g1: LineSegment StartX=30.6341 StartY=28.2329 StartZ=0 EndX=28.207 EndY=29.9963 EndZ=0
    g2: Circle CenterX=29.4206 CenterY=29.1146 CenterZ=0 NormalX=0 NormalY=0 NormalZ=1 AngleXU=0 Radius=2.75
  constraints (7):
    c: Coincident(g0,g-3)
    c: Coincident(g0,g-4)
    c: Coincident(g1,g-3)
    c: Coincident(g1,g-4)
    c: PointOnObject(g2,g1)
    c: PointOnObject(g2,g0)
    c: PointOnObject(g-5,g2)
FEATURE [PartDesign::Pocket] Pocket028
  BaseFeature = -> Pocket027
  Direction = (0,0,-1)
  Length = 0
  Length2 = 5
  Profile = -> Sketch049
  ReferenceAxis = -> Sketch049 [N_Axis]
  Refine = true
  Type = 3
  UpToFace = -> Pocket027 [Face285]
FEATURE [Sketcher::SketchObject] Sketch050
  ExternalGeometry = -> [Pocket028]
  FullyConstrained = true
  MapMode = 5
  Placement = pos=(0,0,-1e-16) rot=(1,0,0;3.14159rad)
  Support = -> [Pocket028]
  sketch-geometry (2):
    g0: Circle CenterX=19.2448 CenterY=-21.8895 CenterZ=0 NormalX=0 NormalY=0 NormalZ=1 AngleXU=0 Radius=18
    g1: Circle CenterX=19.2448 CenterY=-21.8895 CenterZ=0 NormalX=0 NormalY=0 NormalZ=1 AngleXU=0 Radius=23
  constraints (4):
    c: Coincident(g0,g-3)
    c: Coincident(g1,g0)
    c: Diameter(g1) = 46
    c: PointOnObject(g-3,g0)
FEATURE [PartDesign::Pad] Pad038
  BaseFeature = -> Pocket028
  Direction = (0,0,-1)
  Length = 20
  Length2 = 5
  Profile = -> Sketch050
  ReferenceAxis = -> Sketch050 [N_Axis]
  Refine = true
  Type = 4
FEATURE [Part::Feature] Part__Feature  label="540_Motor"
  Placement = pos=(-0.5,1.5,26) rot=(-0.211303,0.691141,-0.691141;2.72511rad)
  shape: bbox 37.93 x 37.93 x 75.14 mm, 145 faces (baked)
FEATURE [Part::Feature] Part__Feature001  label="GearboxPlate_L"
  Placement = pos=(-29.1874,-91.634,75.8) rot=(0,0,1;0.680678rad)
  shape: bbox 87.16 x 102.4 x 14.95 mm, 183 faces (baked)
FEATURE [Part::Feature] Part__Feature002  label="GearboxPlate_R"
  Placement = pos=(-29.2132,-91.6248,59.2) rot=(0,0,1;0.680678rad)
  shape: bbox 87.16 x 102.4 x 14.95 mm, 183 faces (baked)
FEATURE [Mesh::Feature] RightDriveArmV2
FEATURE [Part::Feature] RightDriveArmV2001
  Placement = pos=(-0.699521,-76.5271,18) rot=(0,0,1;1.55334rad)
  shape: bbox 54.01 x 81.69 x 74.72 mm, 4338 faces, 0 solids (baked)
FEATURE [Mesh::Feature] Left_ORV_Pivot_Cover
FEATURE [Part::Feature] Left_ORV_Pivot_Cover001
  shape: bbox 41.54 x 30 x 5.5 mm, 1740 faces, 0 solids (baked)
FEATURE [Sketcher::SketchObject] Sketch051
  ExternalGeometry = -> [Pad038]
  FullyConstrained = false
  MapMode = 5
  Placement = pos=(0,1e-16,5) rot=(0,0,1;0rad)
  Support = -> [Pad038]
  sketch-geometry (11):
    g0: ArcOfCircle CenterX=19.2448 CenterY=21.8895 CenterZ=0 NormalX=0 NormalY=0 NormalZ=1 AngleXU=0 Radius=23 StartAngle=5.26671 EndAngle=8.247
    g1: LineSegment StartX=10.4362 StartY=43.1359 StartZ=0 EndX=25.7652 EndY=32.5622 EndZ=0
    g2: LineSegment StartX=25.7652 StartY=32.5622 StartZ=0 EndX=29.8652 EndY=34.7979 EndZ=0
    g3: LineSegment StartX=29.8652 StartY=34.7979 StartZ=0 EndX=35.3485 EndY=29.2858 EndZ=0
    g4: LineSegment StartX=35.3485 StartY=29.2858 StartZ=0 EndX=32.7588 EndY=25.6869 EndZ=0
    g5: LineSegment StartX=32.7588 StartY=25.6869 StartZ=0 EndX=34.2619 EndY=22.7418 EndZ=0
    g6: LineSegment StartX=34.2619 StartY=22.7418 StartZ=0 EndX=35.4261 EndY=18.2203 EndZ=0
    g7: LineSegment StartX=35.4261 StartY=18.2203 StartZ=0 EndX=35.4261 EndY=14.167 EndZ=0
    g8: LineSegment StartX=35.4261 StartY=14.167 StartZ=0 EndX=34.4233 EndY=10.2784 EndZ=0
    g9: LineSegment StartX=34.4233 StartY=10.2784 StartZ=0 EndX=32.2245 EndY=6.11627 EndZ=0
    g10: LineSegment StartX=32.2245 StartY=6.11627 StartZ=0 EndX=31.3513 EndY=2.33361 EndZ=0
  constraints (14):
    c: Coincident(g0,g-3)
    c: Equal(g0,g-3)
    c: Coincident(g2,g1)
    c: Coincident(g3,g2)
    c: Coincident(g4,g3)
    c: Coincident(g5,g4)
    c: Coincident(g6,g5)
    c: Coincident(g7,g6)
    c: Vertical(g7)
    c: Coincident(g8,g7)
    c: Coincident(g9,g8)
    c: Coincident(g10,g9)
    c: Coincident(g0,g1)
    c: Coincident(g0,g10)
FEATURE [PartDesign::Pad] Pad039
  BaseFeature = -> Pad038
  Direction = (0,0,1)
  Length = 19.2
  Length2 = 10
  Profile = -> Sketch051
  ReferenceAxis = -> Sketch051 [N_Axis]
  Type = 0
FEATURE [Mesh::Feature] ORV_Motor_Gear_Cover
FEATURE [Part::Feature] ORV_Motor_Gear_Cover001
  shape: bbox 32.5 x 29 x 13 mm, 6215 faces, 0 solids (baked)
FEATURE [Part::Feature] ORV_Motor_Gear_Cover001_solid  label="ORV_Motor_Gear_Cover001 (Solid)"
  Placement = pos=(0.700045,-1.31796,77.2205) rot=(0.001677,-0.003531,0.999992;2.16329rad)
  shape: bbox 29.02 x 29.05 x 13.15 mm, 6215 faces (baked)
FEATURE [Sketcher::SketchObject] Sketch052
  ExternalGeometry = -> [Pad039]
  FullyConstrained = true
  MapMode = 5
  Placement = pos=(-2e-16,5e-16,24.2) rot=(0,0,1;0rad)
  Support = -> [Pad039]
  sketch-geometry (2):
    g0: Circle CenterX=19.2448 CenterY=21.8895 CenterZ=0 NormalX=0 NormalY=0 NormalZ=1 AngleXU=0 Radius=23
    g1: Circle CenterX=29.5 CenterY=29 CenterZ=0 NormalX=0 NormalY=0 NormalZ=1 AngleXU=0 Radius=6
  constraints (6):
    c: Equal(g0,g-3)
    c: PointOnObject(g-3,g0)
    c: PointOnObject(g-3,g0)
    c: Diameter(g1) = 12
    c: DistanceX(g1) = 29.5
    c: DistanceY(g1) = 29
FEATURE [PartDesign::Pad] Pad040
  BaseFeature = -> Pad039
  Direction = (0,0,1)
  Length = 12
  Length2 = 10
  Profile = -> Sketch052
  ReferenceAxis = -> Sketch052 [N_Axis]
  Type = 0
FEATURE [Sketcher::SketchObject] Sketch053
  FullyConstrained = true
  MapMode = 5
  Placement = pos=(0,0,24.2) rot=(1,0,0;3.14159rad)
  Support = -> [Pad040]
  sketch-geometry (2):
    g0: Circle CenterX=12.3081 CenterY=-28.1626 CenterZ=0 NormalX=0 NormalY=0 NormalZ=1 AngleXU=0 Radius=1.8
    g1: Circle CenterX=26.1818 CenterY=-7.57899 CenterZ=0 NormalX=0 NormalY=0 NormalZ=1 AngleXU=0 Radius=1.8
  constraints (6):
    c: Diameter(g1) = 3.6
    c: DistanceX(g1) = 26.1818
    c: DistanceY(g1) = -7.57899
    c: Diameter(g0) = 3.6
    c: DistanceX(g0) = 12.3081
    c: DistanceY(g0) = -28.1626
FEATURE [PartDesign::Pocket] Pocket029
  BaseFeature = -> Pad040
  Direction = (0,0,1)
  Length = 13
  Length2 = 5
  Profile = -> Sketch053
  ReferenceAxis = -> Sketch053 [N_Axis]
  Type = 0
FEATURE [Sketcher::SketchObject] Sketch054
  FullyConstrained = true
  MapMode = 5
  Placement = pos=(0,0,24.2) rot=(1,0,0;3.14159rad)
  Support = -> [Pocket029]
  sketch-geometry (1):
    g0: Circle CenterX=19.2679 CenterY=-17.9016 CenterZ=0 NormalX=0 NormalY=0 NormalZ=1 AngleXU=0 Radius=7.5
  constraints (3):
    c: Diameter(g0) = 15
    c: DistanceX(g0) = 19.2679
    c: DistanceY(g0) = -17.9016
FEATURE [PartDesign::Pocket] Pocket030
  BaseFeature = -> Pocket029
  Direction = (0,0,1)
  Length = 10
  Length2 = 5
  Profile = -> Sketch054
  ReferenceAxis = -> Sketch054 [N_Axis]
  Type = 0
FEATURE [PartDesign::Fillet] Fillet020
  Base = -> Pocket030 [Edge848]
  BaseFeature = -> Pocket030
  Radius = 5
  SupportTransform = false
  UseAllEdges = false
FEATURE [Sketcher::SketchObject] Sketch055
  ExternalGeometry = -> [Fillet020]
  FullyConstrained = true
  MapMode = 5
  Placement = pos=(0,0,36.2) rot=(0,0,1;0rad)
  Support = -> [Fillet020]
  sketch-geometry (2):
    g0: Circle CenterX=12.3081 CenterY=28.1626 CenterZ=0 NormalX=0 NormalY=0 NormalZ=1 AngleXU=0 Radius=3
    g1: Circle CenterX=26.1818 CenterY=7.57899 CenterZ=0 NormalX=0 NormalY=0 NormalZ=1 AngleXU=0 Radius=3
  constraints (4):
    c: Coincident(g0,g-4)
    c: Coincident(g1,g-5)
    c: Equal(g1,g0)
    c: Diameter(g1) = 6
FEATURE [PartDesign::Pocket] Pocket031
  BaseFeature = -> Fillet020
  Direction = (0,0,-1)
  Length = 5.8
  Length2 = 5
  Profile = -> Sketch055
  ReferenceAxis = -> Sketch055 [N_Axis]
  Type = 0
FEATURE [PartDesign::Pocket] Pocket032
  BaseFeature = -> Pocket031
  Direction = (0,0,-1)
  Length = 0
  Length2 = 5
  Profile = -> Pocket031 [Face19]
  Refine = true
  Type = 3
  UpToFace = -> Pocket031 [Face18]
FEATURE [Sketcher::SketchObject] Sketch056
  AttachmentOffset = pos=(0,0,-8) rot=(0,0,1;0rad)
  ExternalGeometry = -> [Pocket032]
  FullyConstrained = true
  MapMode = 5
  Placement = pos=(0,0,28.2) rot=(0,0,1;0rad)
  Support = -> [Pocket032]
  sketch-geometry (5):
    g0: Circle CenterX=2.33171 CenterY=42.513 CenterZ=0 NormalX=0 NormalY=0 NormalZ=1 AngleXU=0 Radius=1.8
    g1: LineSegment StartX=10.1265 StartY=43.0048 StartZ=0 EndX=5.28442 EndY=46.5481 EndZ=0
    g2: ArcOfCircle CenterX=2.33171 CenterY=42.513 CenterZ=0 NormalX=0 NormalY=0 NormalZ=1 AngleXU=0 Radius=5 StartAngle=0.939066 EndAngle=3.26279
    g3: LineSegment StartX=-2.63161 StartY=41.9086 StartZ=0 EndX=-1.42264 EndY=31.9819 EndZ=0
    g4: ArcOfCircle CenterX=19.2448 CenterY=21.8895 CenterZ=0 NormalX=0 NormalY=0 NormalZ=1 AngleXU=0 Radius=23 StartAngle=1.97844 EndAngle=2.68733
  constraints (15):
    c: Diameter(g0) = 3.6
    c: PointOnObject(g1,g-3)
    c: Coincident(g2,g0)
    c: DistanceX(g0) = 2.33171
    c: DistanceY(g0) = 42.513
    c: Diameter(g2) = 10
    c: Distance(g1) = 6
    c: PointOnObject(g3,g2)
    c: PointOnObject(g3,g-3)
    c: Distance(g3) = 10
    c: Coincident(g4,g-3)
    c: Tangent(g2,g1) = -1.5708
    c: Tangent(g2,g3) = -1.5708
    c: Coincident(g4,g1)
    c: PointOnObject(g4,g3)
FEATURE [PartDesign::Pad] Pad041
  BaseFeature = -> Pocket032
  Direction = (0,0,1)
  Length = 4
  Length2 = 10
  Profile = -> Sketch056
  ReferenceAxis = -> Sketch056 [N_Axis]
  Reversed = true
  Type = 0
FEATURE [Part::Feature] Blackfoot_motor_mount001_solid001  label="Blackfoot_motor_mount001 (Solid)001"
  Placement = pos=(-27.8205,-8.18653,53) rot=(0,0,-1;0.523599rad)
  shape: bbox 35.12 x 33.98 x 5.85 mm, 1350 faces (baked)
FEATURE [Sketcher::SketchObject] Sketch067
  AttachmentOffset = pos=(0.1,-0.1,-31.2) rot=(0,0,1;0rad)
  FullyConstrained = false
  MapMode = 5
  Placement = pos=(0.1,-0.1,5) rot=(0,0,1;0rad)
  sketch-geometry (5):
    g0: Circle CenterX=2.33171 CenterY=42.513 CenterZ=0 NormalX=0 NormalY=0 NormalZ=1 AngleXU=0 Radius=1.8
    g1: LineSegment StartX=10.1165 StartY=43.1435 StartZ=0 EndX=5.21214 EndY=46.6 EndZ=0
    g2: ArcOfCircle CenterX=2.33171 CenterY=42.513 CenterZ=0 NormalX=0 NormalY=0 NormalZ=1 AngleXU=0 Radius=5 StartAngle=0.956864 EndAngle=3.25076
    g3: LineSegment StartX=-2.63852 StartY=41.9683 StartZ=0 EndX=-1.54897 EndY=32.0278 EndZ=0
    g4: ArcOfCircle CenterX=19.1448 CenterY=21.9895 CenterZ=0 NormalX=0 NormalY=0 NormalZ=1 AngleXU=0 Radius=23 StartAngle=1.97418 EndAngle=2.68995
  constraints (12):
    c: Diameter(g0) = 3.6
    c: Coincident(g2,g0)
    c: DistanceX(g0) = 2.33171
    c: DistanceY(g0) = 42.513
    c: Diameter(g2) = 10
    c: Distance(g1) = 6
    c: PointOnObject(g3,g2)
    c: Distance(g3) = 10
    c: Tangent(g2,g1) = -1.5708
    c: Tangent(g2,g3) = -1.5708
    c: Coincident(g4,g1)
    c: PointOnObject(g4,g3)
FEATURE [PartDesign::Pad] Pad047
  BaseFeature = -> Pad041
  Direction = (0,0,1)
  Length = 6
  Length2 = 10
  Profile = -> Sketch067
  ReferenceAxis = -> Sketch067 [N_Axis]
  Reversed = true
  Type = 0
FEATURE [Sketcher::SketchObject] Sketch068
  AttachmentOffset = pos=(0,0,-4) rot=(0,0,1;0rad)
  ExternalGeometry = -> [Pad047]
  FullyConstrained = true
  MapMode = 5
  Placement = pos=(0,0,32.2) rot=(0,0,1;0rad)
  Support = -> [Pad047]
  sketch-geometry (5):
    g0: LineSegment StartX=20.4188 StartY=-1.08049 StartZ=0 EndX=24.828 EndY=-7.75574 EndZ=0
    g1: Circle CenterX=29 CenterY=-5 CenterZ=0 NormalX=0 NormalY=0 NormalZ=1 AngleXU=0 Radius=1.8
    g2: LineSegment StartX=33.072 StartY=3.50993 StartZ=0 EndX=33.9685 EndY=-4.43967 EndZ=0
    g3: ArcOfCircle CenterX=19.2448 CenterY=21.8895 CenterZ=0 NormalX=0 NormalY=0 NormalZ=1 AngleXU=0 Radius=23 StartAngle=4.76345 EndAngle=5.35737
    g4: ArcOfCircle CenterX=29 CenterY=-5 CenterZ=0 NormalX=0 NormalY=0 NormalZ=1 AngleXU=0 Radius=5 StartAngle=3.72533 EndAngle=6.39549
  constraints (14):
    c: PointOnObject(g0,g-3)
    c: Diameter(g1) = 3.6
    c: PointOnObject(g2,g-3)
    c: Equal(g2,g0)
    c: Distance(g2) = 8
    c: Coincident(g3,g-3)
    c: Coincident(g3,g0)
    c: PointOnObject(g3,g2)
    c: Tangent(g4,g0) = -1.5708
    c: Diameter(g4) = 10
    c: Coincident(g4,g1)
    c: DistanceX(g1) = 29
    c: DistanceY(g1) = -5
    c: Tangent(g4,g2) = 1.5708
FEATURE [PartDesign::Pad] Pad048
  BaseFeature = -> Pad047
  Direction = (0,0,1)
  Length = 8
  Length2 = 10
  Profile = -> Sketch068
  ReferenceAxis = -> Sketch068 [N_Axis]
  Reversed = true
  Type = 0
FEATURE [Sketcher::SketchObject] Sketch069
  AttachmentOffset = pos=(0,0,-17) rot=(0,0,1;0rad)
  ExternalGeometry = -> [Pad048]
  FullyConstrained = true
  MapMode = 5
  Placement = pos=(0,-1e-16,-3) rot=(1,0,0;3.14159rad)
  Support = -> [Pad048]
  sketch-geometry (5):
    g0: Circle CenterX=29 CenterY=5 CenterZ=0 NormalX=0 NormalY=0 NormalZ=1 AngleXU=0 Radius=1.8
    g1: ArcOfCircle CenterX=29 CenterY=5 CenterZ=0 NormalX=0 NormalY=0 NormalZ=1 AngleXU=0 Radius=5 StartAngle=6.17088 EndAngle=8.84104
    g2: LineSegment StartX=33.072 StartY=-3.50993 StartZ=0 EndX=33.9685 EndY=4.43967 EndZ=0
    g3: LineSegment StartX=24.828 StartY=7.75574 StartZ=0 EndX=20.4188 EndY=1.08049 EndZ=0
    g4: ArcOfCircle CenterX=19.2448 CenterY=-21.8895 CenterZ=0 NormalX=0 NormalY=0 NormalZ=1 AngleXU=0 Radius=23 StartAngle=0.925819 EndAngle=1.51973
  constraints (12):
    c: Coincident(g0,g-8)
    c: Coincident(g1,g0)
    c: Coincident(g1,g-5)
    c: Coincident(g1,g-6)
    c: Coincident(g2,g-6)
    c: Coincident(g2,g1)
    c: Coincident(g3,g1)
    c: Coincident(g3,g-4)
    c: Coincident(g4,g-3)
    c: Coincident(g4,g3)
    c: Coincident(g4,g2)
    c: Equal(g0,g-8)
FEATURE [PartDesign::Pad] Pad049
  BaseFeature = -> Pad048
  Direction = (0,0,-1)
  Length = 8
  Length2 = 10
  Profile = -> Sketch069
  ReferenceAxis = -> Sketch069 [N_Axis]
  Reversed = true
  Type = 0
FEATURE [Sketcher::SketchObject] Sketch070
  FullyConstrained = false
  MapMode = 5
  Support = -> [XY_Plane013]
  sketch-geometry (4):
    g0: LineSegment StartX=0 StartY=0 StartZ=0 EndX=93.5609 EndY=0 EndZ=0
    g1: LineSegment StartX=93.5609 StartY=0 StartZ=0 EndX=93.5609 EndY=81.4616 EndZ=0
    g2: LineSegment StartX=93.5609 StartY=81.4616 StartZ=0 EndX=0 EndY=81.4616 EndZ=0
    g3: LineSegment StartX=0 StartY=81.4616 StartZ=0 EndX=0 EndY=0 EndZ=0
  constraints (9):
    c: Coincident(g0,g1)
    c: Coincident(g1,g2)
    c: Coincident(g2,g3)
    c: Coincident(g3,g0)
    c: Horizontal(g0)
    c: Horizontal(g2)
    c: Vertical(g1)
    c: Vertical(g3)
    c: Coincident(g0,g-1)
FEATURE [PartDesign::Pad] Pad050
  Direction = (0,0,1)
  Length = 0.6
  Length2 = 10
  Profile = -> Sketch070
  ReferenceAxis = -> Sketch070 [N_Axis]
  Type = 0
FEATURE [PartDesign::Body] Body012
  Group = -> [Sketch070,Pad050]
  Origin = -> Origin013
  Placement = pos=(-43,-38,68) rot=(0,0,1;0rad)
  Tip = -> Pad050
FEATURE [Sketcher::SketchObject] Sketch071
  FullyConstrained = true
  MapMode = 5
  Placement = pos=(0,0,36.2) rot=(0,0,1;0rad)
  Support = -> [Pad049]
FEATURE [PartDesign::Body] Body011  label="MotorMount"
  BaseFeature = -> Blackfoot_motor_mount001_solid
  Group = -> [BaseFeature003,Sketch046,Pad036,Sketch047,Pad037,Sketch048,Pocket027,Sketch049,Pocket028,Sketch050,Pad038,Sketch051,Pad039,Sketch052,Pad040,Sketch053,Pocket029,Sketch054,Pocket030,Fillet020,Sketch055,Pocket031,Pocket032,Sketch056,Pad041,Sketch067,Pad047,Sketch068,Pad048,Sketch069,Pad049,Sketch071]
  Origin = -> Origin011
  Placement = pos=(-19.5,-20.5,53) rot=(0,0,1;0rad)
  Tip = -> Pad049
FEATURE [Part::FeaturePython] Slice  # WARN: FeaturePython — macro-defined, semantics opaque (R4)
  Base = -> Body011
  Mode = 1
  Tolerance = 0
  Tools = -> [Body012]
FEATURE [Part::FeaturePython] Slice_child2  label="Slice.2"  # WARN: FeaturePython — macro-defined, semantics opaque (R4)
  Base = -> Slice
  FilterType = 1
  Invert = false
  OverrideMaxVal = 0
  WindowFrom = 80
  WindowTo = 100
  items = 2
FEATURE [PartDesign::FeatureBase] BaseFeature005
  BaseFeature = -> Slice_child2
FEATURE [Part::FeaturePython] Slice_child0  label="Slice.0"  # WARN: FeaturePython — macro-defined, semantics opaque (R4)
  Base = -> Slice
  FilterType = 1
  Invert = false
  OverrideMaxVal = 0
  WindowFrom = 80
  WindowTo = 100
  items = 0
FEATURE [PartDesign::FeatureBase] BaseFeature006
  BaseFeature = -> Slice_child0
FEATURE [App::DocumentObjectGroup] GrExplode_Slice  label="Exploded Slice"
  Group = -> [Slice_child0,Slice_child2]
FEATURE [PartDesign::Fillet] Fillet021
  Base = -> BaseFeature006 [Edge32]
  BaseFeature = -> BaseFeature006
  Radius = 1
  SupportTransform = false
  UseAllEdges = false
FEATURE [Sketcher::SketchObject] Sketch072
  ExternalGeometry = -> [BaseFeature005]
  FullyConstrained = true
  MapMode = 5
  Placement = pos=(0,1.1e-15,53) rot=(1,0,0;3.14159rad)
  Support = -> [BaseFeature005]
  sketch-geometry (7):
    g0: LineSegment StartX=4.84802 StartY=10.2871 StartZ=0 EndX=8.01045 EndY=10.0002 EndZ=0
    g1: LineSegment StartX=8.01045 StartY=10.0002 StartZ=0 EndX=9.84021 EndY=12.5954 EndZ=0
    g2: LineSegment StartX=9.84021 StartY=12.5954 StartZ=0 EndX=8.50754 EndY=15.4776 EndZ=0
    g3: LineSegment StartX=8.50754 StartY=15.4776 StartZ=0 EndX=5.34511 EndY=15.7646 EndZ=0
    g4: LineSegment StartX=5.34511 StartY=15.7646 StartZ=0 EndX=3.51535 EndY=13.1694 EndZ=0
    g5: LineSegment StartX=3.51535 StartY=13.1694 StartZ=0 EndX=4.84802 EndY=10.2871 EndZ=0
    g6: Circle CenterX=6.67778 CenterY=12.8824 CenterZ=0 NormalX=0 NormalY=0 NormalZ=1 AngleXU=0 Radius=3.17543
  constraints (15):
    c: Coincident(g0,g1)
    c: Coincident(g1,g2)
    c: Coincident(g2,g3)
    c: Coincident(g3,g4)
    c: Coincident(g4,g5)
    c: Coincident(g5,g0)
    c: Equal(g0, g1-g5) x5
    c: PointOnObject(g0,g6)
    c: PointOnObject(g1,g6)
    c: PointOnObject(g2,g6)
    c: PointOnObject(g3,g6)
    c: PointOnObject(g4,g6)
    c: PointOnObject(g5,g6)
    c: Coincident(g5,g-4)
    c: Coincident(g4,g-4)
FEATURE [PartDesign::Pocket] Pocket033
  BaseFeature = -> BaseFeature005
  Direction = (0,0,1)
  Length = 2.75
  Length2 = 3
  Profile = -> Sketch072
  ReferenceAxis = -> Sketch072 [N_Axis]
  Type = 4
FEATURE [Mesh::Feature] hex_Blackfoot_Rear_Wheel
FEATURE [Mesh::Feature] moyeuxTamyaGrasshopper
FEATURE [Part::Feature] moyeuxTamyaGrasshopper001
  shape: bbox 28.99 x 10 x 28.98 mm, 2398 faces, 0 solids (baked)
FEATURE [Part::Feature] moyeuxTamyaGrasshopper001_solid  label="moyeuxTamyaGrasshopper001 (Solid)"
  shape: bbox 28.99 x 10 x 28.98 mm, 2398 faces (baked)
FEATURE [PartDesign::FeatureBase] BaseFeature007
  BaseFeature = -> moyeuxTamyaGrasshopper001_solid
FEATURE [PartDesign::Body] Body015  label="rear_wheel_adapter"
  BaseFeature = -> moyeuxTamyaGrasshopper001_solid
  Group = -> [BaseFeature007]
  Origin = -> Origin016
  Placement = pos=(-0.247487,-49.1793,-27.2) rot=(-0.281085,0.678598,0.678598;3.68962rad)
  Tip = -> BaseFeature007
FEATURE [Mesh::Feature] Rim__IN_01  label="Rim__IN_original"
FEATURE [Mesh::Feature] Rim_OUT_01  label="Rim_OUT_original001"
FEATURE [Part::Feature] Rim_OUT_01001  label="Rim_OUT_original"
  shape: bbox 55.12 x 55.12 x 23.63 mm, 3456 faces, 0 solids (baked)
FEATURE [Part::Feature] Rim__IN_01001  label="Rim__IN_original001"
  shape: bbox 55.12 x 55.12 x 12.37 mm, 1952 faces, 0 solids (baked)
FEATURE [Part::Feature] Rim_OUT_01001_solid  label="Rim_OUT_original (Solid)"
  Placement = pos=(0,68,0) rot=(0,0,1;0rad)
  shape: bbox 55.12 x 55.12 x 23.63 mm, 3456 faces (baked)
FEATURE [Part::Feature] Rim__IN_01001_solid  label="Rim__IN_original (Solid)"
  shape: bbox 55.12 x 55.12 x 12.37 mm, 1952 faces (baked)
FEATURE [PartDesign::FeatureBase] BaseFeature008
  BaseFeature = -> Rim__IN_01001_solid
FEATURE [PartDesign::FeatureBase] BaseFeature009
  BaseFeature = -> Rim_OUT_01001_solid
FEATURE [PartDesign::Body] Body017  label="Rim_out"
  BaseFeature = -> Rim_OUT_01001_solid
  Group = -> [BaseFeature009]
  Origin = -> Origin018
  Tip = -> BaseFeature009
FEATURE [App::Part] Part002  label="Rimout"
  Group = -> [Rim_OUT_01001_solid,Body017,Rim_OUT_01001,Rim_OUT_01]
  Origin = -> Origin020
  Placement = pos=(-20.7361,-49.1742,-35.7) rot=(-0.793353,-0.608761,0;3.14159rad)
FEATURE [Sketcher::SketchObject] Sketch073
  FullyConstrained = false
  MapMode = 5
  Placement = pos=(0,0,32.2) rot=(0,0,1;0rad)
  Support = -> [BaseFeature008]
  sketch-geometry (4):
    g0: LineSegment StartX=40.8798 StartY=84.5784 StartZ=0 EndX=89.517 EndY=84.5784 EndZ=0
    g1: LineSegment StartX=89.517 StartY=84.5784 StartZ=0 EndX=89.517 EndY=44.058 EndZ=0
    g2: LineSegment StartX=89.517 StartY=44.058 StartZ=0 EndX=40.8798 EndY=44.058 EndZ=0
    g3: LineSegment StartX=40.8798 StartY=44.058 StartZ=0 EndX=40.8798 EndY=84.5784 EndZ=0
  constraints (8):
    c: Coincident(g0,g1)
    c: Coincident(g1,g2)
    c: Coincident(g2,g3)
    c: Coincident(g3,g0)
    c: Horizontal(g0)
    c: Horizontal(g2)
    c: Vertical(g1)
    c: Vertical(g3)
FEATURE [PartDesign::Pocket] Pocket034
  BaseFeature = -> BaseFeature008
  Direction = (0,0,-1)
  Length = 5
  Length2 = 5
  Profile = -> Sketch073
  ReferenceAxis = -> Sketch073 [N_Axis]
  Refine = true
  Reversed = true
  Type = 0
FEATURE [Sketcher::SketchObject] Sketch074
  ExternalGeometry = -> [Pocket034]
  FullyConstrained = true
  MapMode = 5
  Placement = pos=(0,0,32.2) rot=(0,0,1;0rad)
  Support = -> [Pocket034]
  sketch-geometry (9):
    g0: Circle CenterX=54.1829 CenterY=61.8618 CenterZ=0 NormalX=0 NormalY=0 NormalZ=1 AngleXU=0 Radius=3.75
    g1: GeomPoint X=63.9424 Y=63.9424 Z=0
    g2: Circle CenterX=63.9424 CenterY=63.9424 CenterZ=0 NormalX=0 NormalY=0 NormalZ=1 AngleXU=0 Radius=2.1
    g3: Circle CenterX=62.8954 CenterY=54.0019 CenterZ=0 NormalX=0 NormalY=0 NormalZ=1 AngleXU=0 Radius=3.75
    g4: Circle CenterX=73.1116 CenterY=59.8214 CenterZ=0 NormalX=0 NormalY=0 NormalZ=1 AngleXU=0 Radius=3.75
    g5: Circle CenterX=70.6679 CenterY=71.3243 CenterZ=0 NormalX=0 NormalY=0 NormalZ=1 AngleXU=0 Radius=3.75
    g6: Circle CenterX=59.0139 CenterY=72.5598 CenterZ=0 NormalX=0 NormalY=0 NormalZ=1 AngleXU=0 Radius=3.75
    g7: Circle CenterX=63.9424 CenterY=63.9424 CenterZ=0 NormalX=0 NormalY=0 NormalZ=1 AngleXU=0 Radius=4.5
    g8: Circle CenterX=63.9424 CenterY=63.9424 CenterZ=0 NormalX=0 NormalY=0 NormalZ=1 AngleXU=0 Radius=2.25
  constraints (23):
    c: Diameter(g0) = 7.5
    c: DistanceX(g0) = 54.1829
    c: DistanceY(g0) = 61.8618
    c: Coincident(g2,g1)
    c: PointOnObject(g-3,g2)
    c: PointOnObject(g-6,g2)
    c: PointOnObject(g-4,g2)
    c: Equal(g3,g0)
    c: DistanceX(g3) = 62.8954
    c: DistanceY(g3) = 54.0019
    c: Equal(g6,g5)
    c: Equal(g5,g4)
    c: Equal(g4,g3)
    c: DistanceX(g4) = 73.1116
    c: DistanceY(g4) = 59.8214
    c: DistanceX(g5) = 70.6679
    c: DistanceY(g5) = 71.3243
    c: DistanceX(g6) = 59.0139
    c: DistanceY(g6) = 72.5598
    c: Coincident(g7,g1)
    c: Coincident(g8,g7)
    c: Diameter(g7) = 9
    c: Diameter(g8) = 4.5
FEATURE [PartDesign::Pad] Pad051
  BaseFeature = -> Pocket034
  Direction = (0,0,1)
  Length = 2.2
  Length2 = 8.35
  Profile = -> Sketch074
  ReferenceAxis = -> Sketch074 [N_Axis]
  Type = 4
FEATURE [Sketcher::SketchObject] Sketch075
  ExternalGeometry = -> [Pad051]
  FullyConstrained = true
  MapMode = 5
  Placement = pos=(0,0,23.8306) rot=(1,0,0;3.14159rad)
  Support = -> [Pad051]
  sketch-geometry (21):
    g0: LineSegment StartX=56.9424 StartY=-46.9244 StartZ=0 EndX=52.7043 EndY=-49.3712 EndZ=0
    g1: LineSegment StartX=52.7043 StartY=-49.3712 StartZ=0 EndX=52.7043 EndY=-54.2649 EndZ=0
    g2: LineSegment StartX=52.7043 StartY=-54.2649 StartZ=0 EndX=56.9424 EndY=-56.7118 EndZ=0
    g3: LineSegment StartX=56.9424 StartY=-56.7118 StartZ=0 EndX=61.1805 EndY=-54.2649 EndZ=0
    g4: LineSegment StartX=61.1805 StartY=-54.2649 StartZ=0 EndX=61.1805 EndY=-49.3712 EndZ=0
    g5: LineSegment StartX=61.1805 StartY=-49.3712 StartZ=0 EndX=56.9424 EndY=-46.9244 EndZ=0
    g6: Circle CenterX=56.9424 CenterY=-51.8181 CenterZ=0 NormalX=0 NormalY=0 NormalZ=1 AngleXU=0 Radius=4.89371
    g7: LineSegment StartX=82.1805 StartY=-61.4956 StartZ=0 EndX=77.9424 EndY=-59.0487 EndZ=0
    g8: LineSegment StartX=77.9424 StartY=-59.0487 StartZ=0 EndX=73.7043 EndY=-61.4956 EndZ=0
    g9: LineSegment StartX=73.7043 StartY=-61.4956 StartZ=0 EndX=73.7043 EndY=-66.3893 EndZ=0
    g10: LineSegment StartX=73.7043 StartY=-66.3893 StartZ=0 EndX=77.9424 EndY=-68.8361 EndZ=0
    g11: LineSegment StartX=77.9424 StartY=-68.8361 StartZ=0 EndX=82.1805 EndY=-66.3893 EndZ=0
    g12: LineSegment StartX=82.1805 StartY=-66.3893 StartZ=0 EndX=82.1805 EndY=-61.4956 EndZ=0
    g13: Circle CenterX=77.9424 CenterY=-63.9424 CenterZ=0 NormalX=0 NormalY=0 NormalZ=1 AngleXU=0 Radius=4.89371
    g14: LineSegment StartX=52.7043 StartY=-78.5136 StartZ=0 EndX=56.9424 EndY=-80.9605 EndZ=0
    g15: LineSegment StartX=56.9424 StartY=-80.9605 StartZ=0 EndX=61.1805 EndY=-78.5136 EndZ=0
    g16: LineSegment StartX=61.1805 StartY=-78.5136 StartZ=0 EndX=61.1805 EndY=-73.6199 EndZ=0
    g17: LineSegment StartX=61.1805 StartY=-73.6199 StartZ=0 EndX=56.9424 EndY=-71.1731 EndZ=0
    g18: LineSegment StartX=56.9424 StartY=-71.1731 StartZ=0 EndX=52.7043 EndY=-73.6199 EndZ=0
    g19: LineSegment StartX=52.7043 StartY=-73.6199 StartZ=0 EndX=52.7043 EndY=-78.5136 EndZ=0
    g20: Circle CenterX=56.9424 CenterY=-76.0668 CenterZ=0 NormalX=0 NormalY=0 NormalZ=1 AngleXU=0 Radius=4.89371
  constraints (45):
    c: Coincident(g0,g1)
    c: Coincident(g1,g2)
    c: Coincident(g2,g3)
    c: Coincident(g3,g4)
    c: Coincident(g4,g5)
    c: Coincident(g5,g0)
    c: Equal(g0, g1-g5) x5
    c: PointOnObject(g0,g6)
    c: PointOnObject(g1,g6)
    c: PointOnObject(g2,g6)
    c: PointOnObject(g3,g6)
    c: PointOnObject(g4,g6)
    c: PointOnObject(g5,g6)
    c: Coincident(g7,g8)
    c: Coincident(g8,g9)
    c: Coincident(g9,g10)
    c: Coincident(g10,g11)
    c: Coincident(g11,g12)
    c: Coincident(g12,g7)
    c: Equal(g7, g8-g12) x5
    c: PointOnObject(g7,g13)
    c: PointOnObject(g8,g13)
    c: PointOnObject(g9,g13)
    c: PointOnObject(g10,g13)
    c: PointOnObject(g11,g13)
    c: PointOnObject(g12,g13)
    c: Coincident(g14,g15)
    c: Coincident(g15,g16)
    c: Coincident(g16,g17)
    c: Coincident(g17,g18)
    c: Coincident(g18,g19)
    c: Coincident(g19,g14)
    c: Equal(g14, g15-g19) x5
    c: PointOnObject(g14,g20)
    c: PointOnObject(g15,g20)
    c: PointOnObject(g16,g20)
    c: PointOnObject(g17,g20)
    c: PointOnObject(g18,g20)
    c: PointOnObject(g19,g20)
    c: Coincident(g0,g-5)
    c: Coincident(g0,g-4)
    c: Coincident(g7,g-8)
    c: Coincident(g11,g-8)
    c: Coincident(g14,g-10)
    c: Coincident(g14,g-11)
FEATURE [PartDesign::Pad] Pad052
  BaseFeature = -> Pad051
  Direction = (0,0,-1)
  Length = 10
  Length2 = 10
  Profile = -> Sketch075
  ReferenceAxis = -> Sketch075 [N_Axis]
  Refine = true
  Type = 3
  UpToFace = -> Pad051 [Face439]
FEATURE [Mesh::Feature] Tire_Airless_02
FEATURE [Part::Feature] Tire_Airless_02001
  shape: bbox 123.4 x 123.4 x 40 mm, 18470 faces, 0 solids (baked)
FEATURE [Part::Feature] Tire_Airless_02001_solid  label="Tire_Airless_02001 (Solid)"
  shape: bbox 123.4 x 123.4 x 40 mm, 18470 faces (baked)
FEATURE [PartDesign::FeatureBase] BaseFeature010
  BaseFeature = -> Tire_Airless_02001_solid
FEATURE [PartDesign::Body] Body018  label="Wheel_outer"
  BaseFeature = -> Tire_Airless_02001_solid
  Group = -> [BaseFeature010]
  Origin = -> Origin022
  Placement = pos=(-96.8011,-93.187,-59) rot=(0,0,-1;0.261799rad)
  Tip = -> BaseFeature010
FEATURE [App::MeasureDistance] Distance001  label="Distance: 10,52 mm"
  Distance = 10.5244
  P1 = (-25.1162,34.4162,-42.7849)
  P2 = (-35.6394,34.27,-42.7162)
FEATURE [App::MeasureDistance] Distance002  label="Distance: 4,23 mm"
  Distance = 4.23076
  P1 = (-35.6394,34.1435,-43.4043)
  P2 = (-35.6394,30.2433,-41.7649)
FEATURE [Sketcher::SketchObject] Sketch076
  ExternalGeometry = -> [Pad052]
  FullyConstrained = true
  MapMode = 5
  Placement = pos=(0,0,23.8306) rot=(1,0,0;3.14159rad)
  Support = -> [Pad052]
  sketch-geometry (2):
    g0: Circle CenterX=63.9424 CenterY=-63.9424 CenterZ=0 NormalX=0 NormalY=0 NormalZ=1 AngleXU=0 Radius=2.7
    g1: Circle CenterX=63.9424 CenterY=-63.9424 CenterZ=0 NormalX=0 NormalY=0 NormalZ=1 AngleXU=0 Radius=2.1
  constraints (5):
    c: Diameter(g0) = 5.4
    c: Coincident(g1,g0)
    c: PointOnObject(g-3,g1)
    c: PointOnObject(g-4,g1)
    c: PointOnObject(g-5,g1)
FEATURE [PartDesign::Pocket] Pocket035
  BaseFeature = -> Pad052
  Direction = (0,0,1)
  Length = 11
  Length2 = 5
  Profile = -> Sketch076
  ReferenceAxis = -> Sketch076 [N_Axis]
  Type = 0
FEATURE [PartDesign::Body] Body016  label="Rim_In"
  BaseFeature = -> Rim__IN_01001_solid
  Group = -> [BaseFeature008,Sketch073,Pocket034,Sketch074,Pad051,Sketch075,Pad052,Sketch076,Pocket035]
  Origin = -> Origin017
  Tip = -> Pocket035
FEATURE [App::Part] Part001  label="RimIn"
  Group = -> [Body016,Rim__IN_01,Rim__IN_01001_solid,Rim__IN_01001]
  Origin = -> Origin019
  Placement = pos=(-65.88,-127.54,-59.47) rot=(0,0,1;0.26337rad)
FEATURE [App::Part] Part003  label="Wheel"
  Group = -> [Tire_Airless_02,Tire_Airless_02001,Part002,Part001,Tire_Airless_02001_solid,Body018]
  Origin = -> Origin021
FEATURE [App::MeasureDistance] Distance003  label="Distance: 15,87 mm"
  Distance = 15.8708
  P1 = (-35.6394,39.4058,-45.826)
  P2 = (-35.6394,24.9356,-39.3071)
FEATURE [Sketcher::SketchObject] Sketch077
  ExternalGeometry = -> [Pocket033]
  FullyConstrained = true
  MapMode = 5
  Placement = pos=(0,7e-16,33) rot=(1,0,0;3.14159rad)
  Support = -> [Pocket033]
  sketch-geometry (2):
    g0: Circle CenterX=-0.255171 CenterY=-1.38953 CenterZ=0 NormalX=0 NormalY=0 NormalZ=1 AngleXU=0 Radius=18
    g1: Circle CenterX=-0.255171 CenterY=-1.38953 CenterZ=0 NormalX=0 NormalY=0 NormalZ=1 AngleXU=0 Radius=18.1
  constraints (5):
    c: Coincident(g0,g-3)
    c: Equal(g0,g-3)
    c: Coincident(g1,g0)
    c: Diameter(g1) = 36.2
    c: Diameter(g0) = 36
FEATURE [PartDesign::Pocket] Pocket036
  BaseFeature = -> Pocket033
  Direction = (0,0,1)
  Length = 0
  Length2 = 5
  Profile = -> Sketch077
  ReferenceAxis = -> Sketch077 [N_Axis]
  Refine = true
  Type = 3
  UpToFace = -> Pocket033 [Face272]
FEATURE [PartDesign::Pocket] Pocket037
  BaseFeature = -> Pocket036
  Direction = (0,0,-1)
  Length = 6
  Length2 = 5
  Profile = -> Pocket036 [Face8]
  Type = 0
FEATURE [PartDesign::Pocket] Pocket038
  BaseFeature = -> Fillet021
  Direction = (0,0,-1)
  Length = 5
  Length2 = 5
  Profile = -> Fillet021 [Face9]
  Type = 0
FEATURE [PartDesign::Body] Body014  label="MotorMount2"
  BaseFeature = -> Slice_child0
  Group = -> [BaseFeature006,Fillet021,Pocket038]
  Origin = -> Origin015
  Tip = -> Pocket038
FEATURE [Sketcher::SketchObject] Sketch078
  AttachmentOffset = pos=(0,0,-3) rot=(0,0,1;0rad)
  ExternalGeometry = -> [Pocket037]
  FullyConstrained = true
  MapMode = 5
  Placement = pos=(0,7e-16,36) rot=(1,0,0;3.14159rad)
  Support = -> [Pocket037]
  sketch-geometry (16):
    g0: LineSegment StartX=-6.25517 StartY=20.8141 StartZ=0 EndX=5.74483 EndY=20.8141 EndZ=0
    g1: LineSegment StartX=5.74483 StartY=20.8141 StartZ=0 EndX=5.74483 EndY=28.8141 EndZ=0
    g2: LineSegment StartX=5.74483 StartY=28.8141 StartZ=0 EndX=-6.25517 EndY=28.8141 EndZ=0
    g3: LineSegment StartX=-6.25517 StartY=28.8141 StartZ=0 EndX=-6.25517 EndY=20.8141 EndZ=0
    g4: LineSegment StartX=-6.25517 StartY=-23.5931 StartZ=0 EndX=5.74483 EndY=-23.5931 EndZ=0
    g5: LineSegment StartX=5.74483 StartY=-23.5931 StartZ=0 EndX=5.74483 EndY=-31.5931 EndZ=0
    g6: LineSegment StartX=5.74483 StartY=-31.5931 StartZ=0 EndX=-6.25517 EndY=-31.5931 EndZ=0
    g7: LineSegment StartX=-6.25517 StartY=-31.5931 StartZ=0 EndX=-6.25517 EndY=-23.5931 EndZ=0
    g8: LineSegment StartX=21.9484 StartY=-7.38954 StartZ=0 EndX=29.9484 EndY=-7.38954 EndZ=0
    g9: LineSegment StartX=29.9484 StartY=-7.38954 StartZ=0 EndX=29.9484 EndY=4.61046 EndZ=0
    g10: LineSegment StartX=29.9484 StartY=4.61046 StartZ=0 EndX=21.9484 EndY=4.61046 EndZ=0
    g11: LineSegment StartX=21.9484 StartY=4.61046 StartZ=0 EndX=21.9484 EndY=-7.38954 EndZ=0
    g12: LineSegment StartX=-22.4588 StartY=-7.38953 StartZ=0 EndX=-30.4588 EndY=-7.38953 EndZ=0
    g13: LineSegment StartX=-30.4588 StartY=-7.38953 StartZ=0 EndX=-30.4588 EndY=4.61047 EndZ=0
    g14: LineSegment StartX=-30.4588 StartY=4.61047 StartZ=0 EndX=-22.4588 EndY=4.61047 EndZ=0
    g15: LineSegment StartX=-22.4588 StartY=4.61047 StartZ=0 EndX=-22.4588 EndY=-7.38953 EndZ=0
  constraints (48):
    c: Coincident(g0,g1)
    c: Coincident(g1,g2)
    c: Coincident(g2,g3)
    c: Coincident(g3,g0)
    c: Horizontal(g0)
    c: Horizontal(g2)
    c: Vertical(g1)
    c: Vertical(g3)
    c: PointOnObject(g0,g-3)
    c: Distance(g0) = 12
    c: PointOnObject(g0,g-3)
    c: Distance(g1) = 8
    c: Coincident(g4,g5)
    c: Coincident(g5,g6)
    c: Coincident(g6,g7)
    c: Coincident(g7,g4)
    c: Horizontal(g4)
    c: Horizontal(g6)
    c: Vertical(g5)
    c: Vertical(g7)
    c: PointOnObject(g4,g-3)
    c: Coincident(g8,g9)
    c: Coincident(g9,g10)
    c: Coincident(g10,g11)
    c: Coincident(g11,g8)
    c: Horizontal(g8)
    c: Horizontal(g10)
    c: Vertical(g9)
    c: Vertical(g11)
    c: PointOnObject(g8,g-3)
    c: Coincident(g12,g13)
    c: Coincident(g13,g14)
    c: Coincident(g14,g15)
    c: Coincident(g15,g12)
    c: Horizontal(g12)
    c: Horizontal(g14)
    c: Vertical(g13)
    c: Vertical(g15)
    c: PointOnObject(g12,g-3)
    c: PointOnObject(g14,g-3)
    c: PointOnObject(g10,g-3)
    c: PointOnObject(g4,g-3)
    c: Equal(g10,g5)
    c: Equal(g5,g1)
    c: Equal(g1,g14)
    c: Distance(g6) = 12
    c: Distance(g9) = 12
    c: Distance(g13) = 12
FEATURE [PartDesign::Pad] Pad053
  BaseFeature = -> Pocket037
  Direction = (0,0,-1)
  Length = 12
  Length2 = 10
  Profile = -> Sketch078
  ReferenceAxis = -> Sketch078 [N_Axis]
  Reversed = true
  Type = 0
FEATURE [Sketcher::SketchObject] Sketch079
  ExternalGeometry = -> [Pad053]
  FullyConstrained = true
  MapMode = 5
  Placement = pos=(0,0,36) rot=(1,0,0;3.14159rad)
  Support = -> [Pad053]
  sketch-geometry (24):
    g0: LineSegment StartX=-4.00517 StartY=25.6105 StartZ=0 EndX=3.49483 EndY=25.6105 EndZ=0
    g1: LineSegment StartX=3.49483 StartY=25.6105 StartZ=0 EndX=3.49483 EndY=21.6105 EndZ=0
    g2: LineSegment StartX=3.49483 StartY=21.6105 StartZ=0 EndX=-4.00517 EndY=21.6105 EndZ=0
    g3: LineSegment StartX=-4.00517 StartY=21.6105 StartZ=0 EndX=-4.00517 EndY=25.6105 EndZ=0
    g4: LineSegment StartX=-4.00517 StartY=21.6105 StartZ=0 EndX=-4.00517 EndY=21.3027 EndZ=0
    g5: LineSegment StartX=3.49483 StartY=21.6105 StartZ=0 EndX=3.49483 EndY=21.3027 EndZ=0
    g6: LineSegment StartX=22.7448 StartY=2.36046 StartZ=0 EndX=26.7448 EndY=2.36046 EndZ=0
    g7: LineSegment StartX=26.7448 StartY=2.36046 StartZ=0 EndX=26.7448 EndY=-5.13954 EndZ=0
    g8: LineSegment StartX=26.7448 StartY=-5.13954 StartZ=0 EndX=22.7448 EndY=-5.13954 EndZ=0
    g9: LineSegment StartX=22.7448 StartY=-5.13954 StartZ=0 EndX=22.7448 EndY=2.36046 EndZ=0
    g10: LineSegment StartX=-4.00517 StartY=-24.3895 StartZ=0 EndX=3.49483 EndY=-24.3895 EndZ=0
    g11: LineSegment StartX=3.49483 StartY=-24.3895 StartZ=0 EndX=3.49483 EndY=-28.3895 EndZ=0
    g12: LineSegment StartX=3.49483 StartY=-28.3895 StartZ=0 EndX=-4.00517 EndY=-28.3895 EndZ=0
    g13: LineSegment StartX=-4.00517 StartY=-28.3895 StartZ=0 EndX=-4.00517 EndY=-24.3895 EndZ=0
    g14: LineSegment StartX=-27.2552 StartY=2.36047 StartZ=0 EndX=-23.2552 EndY=2.36047 EndZ=0
    g15: LineSegment StartX=-23.2552 StartY=2.36047 StartZ=0 EndX=-23.2552 EndY=-5.13953 EndZ=0
    g16: LineSegment StartX=-23.2552 StartY=-5.13953 StartZ=0 EndX=-27.2552 EndY=-5.13953 EndZ=0
    g17: LineSegment StartX=-27.2552 StartY=-5.13953 StartZ=0 EndX=-27.2552 EndY=2.36047 EndZ=0
    g18: LineSegment StartX=22.7448 StartY=2.36046 StartZ=0 EndX=22.4371 EndY=2.36046 EndZ=0
    g19: LineSegment StartX=22.7448 StartY=-5.13954 StartZ=0 EndX=22.4371 EndY=-5.13954 EndZ=0
    g20: LineSegment StartX=3.49483 StartY=-24.3895 StartZ=0 EndX=3.49483 EndY=-24.0818 EndZ=0
    g21: LineSegment StartX=-4.00517 StartY=-24.3895 StartZ=0 EndX=-4.00517 EndY=-24.0818 EndZ=0
    g22: LineSegment StartX=-23.2552 StartY=-5.13953 StartZ=0 EndX=-22.9474 EndY=-5.13953 EndZ=0
    g23: LineSegment StartX=-23.2552 StartY=2.36047 StartZ=0 EndX=-22.9474 EndY=2.36047 EndZ=0
  constraints (72):
    c: Coincident(g0,g1)
    c: Coincident(g1,g2)
    c: Coincident(g2,g3)
    c: Coincident(g3,g0)
    c: Horizontal(g0)
    c: Horizontal(g2)
    c: Vertical(g1)
    c: Vertical(g3)
    c: Distance(g1) = 4
    c: Tangent(g2,g-12)
    c: Distance(g0) = 7.5
    c: Coincident(g4,g2)
    c: PointOnObject(g4,g-12)
    c: Vertical(g4)
    c: Coincident(g5,g1)
    c: PointOnObject(g5,g-12)
    c: Equal(g5,g4)
    c: Vertical(g5)
    c: Coincident(g6,g7)
    c: Coincident(g7,g8)
    c: Coincident(g8,g9)
    c: Coincident(g9,g6)
    c: Horizontal(g6)
    c: Horizontal(g8)
    c: Vertical(g7)
    c: Vertical(g9)
    c: Coincident(g10,g11)
    c: Coincident(g11,g12)
    c: Coincident(g12,g13)
    c: Coincident(g13,g10)
    c: Horizontal(g10)
    c: Horizontal(g12)
    c: Vertical(g11)
    c: Vertical(g13)
    c: Coincident(g14,g15)
    c: Coincident(g15,g16)
    c: Coincident(g16,g17)
    c: Coincident(g17,g14)
    c: Horizontal(g14)
    c: Horizontal(g16)
    c: Vertical(g15)
    c: Vertical(g17)
    c: Tangent(g15,g-12)
    c: Tangent(g9,g-12)
    c: Tangent(g10,g-12)
    c: Coincident(g18,g6)
    c: PointOnObject(g18,g-12)
    c: Horizontal(g18)
    c: Coincident(g19,g8)
    c: PointOnObject(g19,g-12)
    c: Horizontal(g19)
    c: Coincident(g20,g10)
    c: PointOnObject(g20,g-12)
    c: Vertical(g20)
    c: Coincident(g21,g10)
    c: PointOnObject(g21,g-12)
    c: Vertical(g21)
    c: Coincident(g22,g15)
    c: PointOnObject(g22,g-12)
    c: Horizontal(g22)
    c: Coincident(g23,g14)
    c: PointOnObject(g23,g-12)
    c: Horizontal(g23)
    c: Equal(g23,g22)
    c: Equal(g19,g18)
    c: Equal(g20,g21)
    c: Distance(g10) = 7.5
    c: Distance(g9) = 7.5
    c: Distance(g15) = 7.5
    c: Distance(g6) = 4
    c: Distance(g11) = 4
    c: Distance(g16) = 4
FEATURE [PartDesign::Pocket] Pocket039
  BaseFeature = -> Pad053
  Direction = (0,0,1)
  Length = 6
  Length2 = 5
  Profile = -> Sketch079
  ReferenceAxis = -> Sketch079 [N_Axis]
  Type = 0
FEATURE [Sketcher::SketchObject] Sketch080
  AttachmentOffset = pos=(0,0,-3) rot=(0,0,1;0rad)
  ExternalGeometry = -> [Pocket039]
  FullyConstrained = true
  MapMode = 5
  Placement = pos=(0,-25.8141,-1e-16) rot=(1,0,0;1.5708rad)
  Support = -> [Pocket039]
  sketch-geometry (7):
    g0: LineSegment StartX=-0.255171 StartY=46.3301 StartZ=0 EndX=-4.00517 EndY=44.1651 EndZ=0
    g1: LineSegment StartX=-4.00517 StartY=44.1651 StartZ=0 EndX=-4.00517 EndY=39.8349 EndZ=0
    g2: LineSegment StartX=-4.00517 StartY=39.8349 StartZ=0 EndX=-0.255171 EndY=37.6699 EndZ=0
    g3: LineSegment StartX=-0.255171 StartY=37.6699 StartZ=0 EndX=3.49483 EndY=39.8349 EndZ=0
    g4: LineSegment StartX=3.49483 StartY=39.8349 StartZ=0 EndX=3.49483 EndY=44.1651 EndZ=0
    g5: LineSegment StartX=3.49483 StartY=44.1651 StartZ=0 EndX=-0.255171 EndY=46.3301 EndZ=0
    g6: Circle CenterX=-0.255171 CenterY=42 CenterZ=0 NormalX=0 NormalY=0 NormalZ=1 AngleXU=0 Radius=4.33013
  constraints (21):
    c: Coincident(g1,g2)
    c: Coincident(g2,g3)
    c: Coincident(g4,g5)
    c: Coincident(g5,g0)
    c: Equal(g0, g1-g5) x5
    c: PointOnObject(g1,g6)
    c: PointOnObject(g2,g6)
    c: PointOnObject(g4,g6)
    c: PointOnObject(g5,g6)
    c: Distance(g0,g3) = 8.66025
    c: Distance(g4,g2) = 7.5
    c: Coincident(g4,g3)
    c: PointOnObject(g3,g6)
    c: Coincident(g0,g1)
    c: PointOnObject(g0,g6)
    c: PointOnObject(g-4,g1)
    c: PointOnObject(g-5,g4)
    c: Vertical(g4)
    c: Distance(g-4,g0) = 2.16506
    c: Distance(g-5,g3) = 2.16506
    c: PointOnObject(g6,g-4)
FEATURE [PartDesign::Pocket] Pocket040
  BaseFeature = -> Pocket039
  Direction = (0,1,-2e-16)
  Length = 4.2
  Length2 = 5
  Profile = -> Sketch080
  ReferenceAxis = -> Sketch080 [N_Axis]
  Type = 0
FEATURE [Sketcher::SketchObject] Sketch081
  ExternalGeometry = -> [Pocket040]
  FullyConstrained = true
  MapMode = 5
  Placement = pos=(0,-28.8141,6e-16) rot=(1,0,0;1.5708rad)
  Support = -> [Pocket040]
  sketch-geometry (3):
    g0: LineSegment StartX=-6.25517 StartY=36 StartZ=0 EndX=5.74483 EndY=48 EndZ=0
    g1: LineSegment StartX=-6.25517 StartY=48 StartZ=0 EndX=5.74483 EndY=36 EndZ=0
    g2: Circle CenterX=-0.255171 CenterY=42 CenterZ=0 NormalX=0 NormalY=0 NormalZ=1 AngleXU=0 Radius=2.35
  constraints (7):
    c: Coincident(g0,g-3)
    c: Coincident(g0,g-4)
    c: Coincident(g1,g-3)
    c: Coincident(g1,g-4)
    c: PointOnObject(g2,g1)
    c: PointOnObject(g2,g0)
    c: Diameter(g2) = 4.7
FEATURE [PartDesign::Pocket] Pocket041
  BaseFeature = -> Pocket040
  Direction = (0,1,-2e-16)
  Length = 65
  Length2 = 5
  Profile = -> Sketch081
  ReferenceAxis = -> Sketch081 [N_Axis]
  Type = 0
FEATURE [PartDesign::Body] Body013  label="MotorMount1"
  BaseFeature = -> Slice_child2
  Group = -> [BaseFeature005,Sketch072,Pocket033,Sketch077,Pocket036,Pocket037,Sketch078,Pad053,Sketch079,Pocket039,Sketch080,Pocket040,Sketch081,Pocket041]
  Origin = -> Origin014
  Tip = -> Pocket041
FEATURE [App::Part] Part  label="BlackFoot"
  Group = -> [Part__Feature,Part__Feature001,Part__Feature002,RightDriveArmV2001,Left_ORV_Pivot_Cover001,ORV_Motor_Gear_Cover001_solid,Body013,Body011,Blackfoot_motor_mount001_solid,Slice_child2,Slice,Body012,Slice_child0,Body014,moyeuxTamyaGrasshopper001_solid,Body015,Part003]
  Origin = -> Origin012
  Placement = pos=(0,0,0) rot=(-0.694747,-0.186157,-0.694747;3.50969rad)
